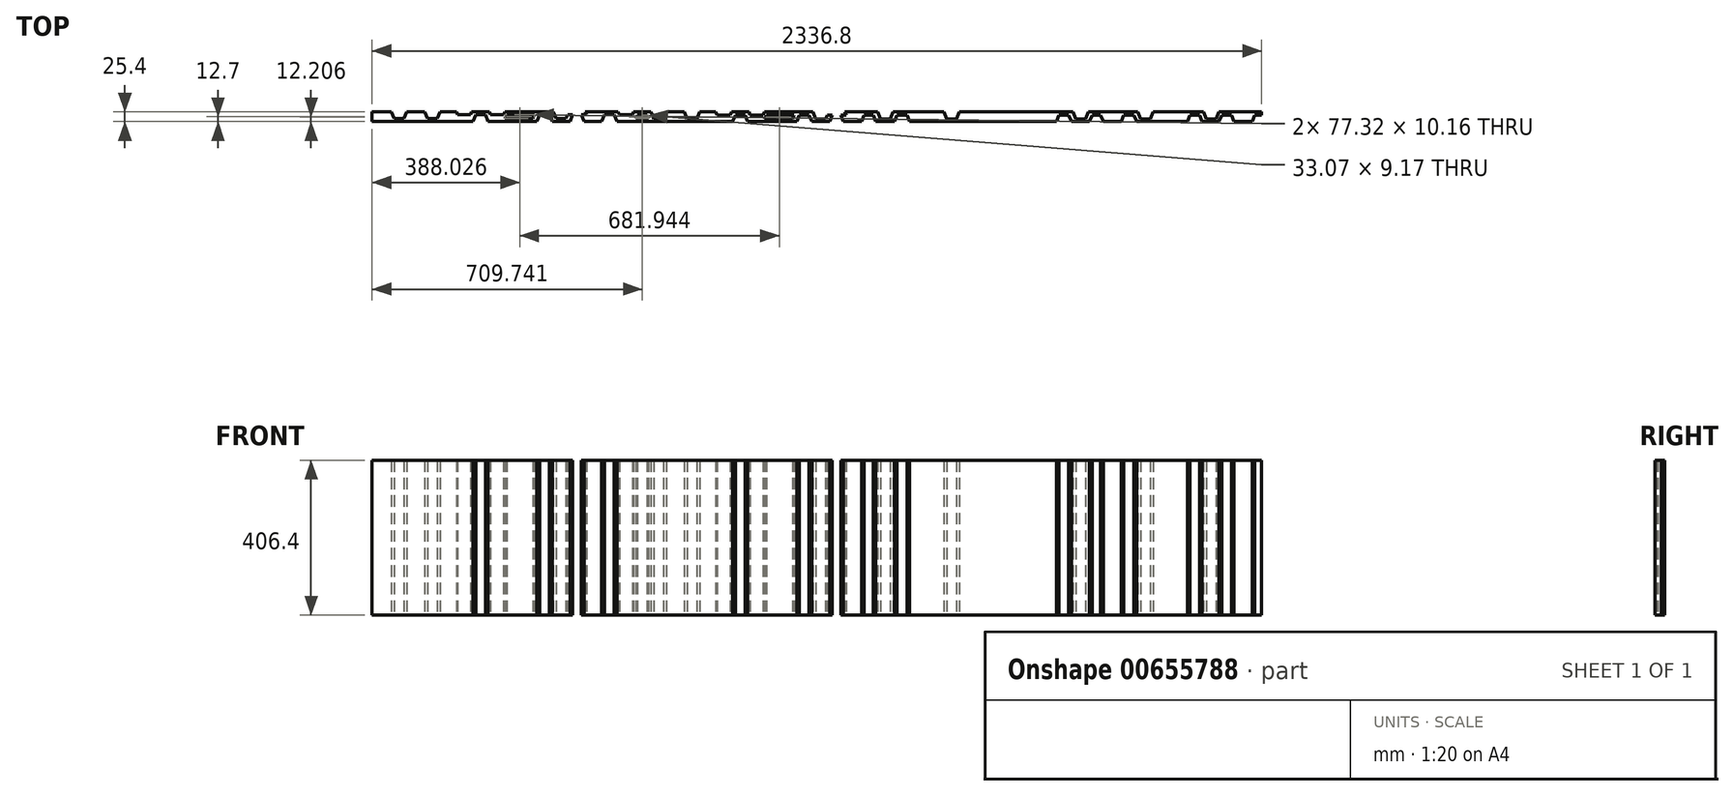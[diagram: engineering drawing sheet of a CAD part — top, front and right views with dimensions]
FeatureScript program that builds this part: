
annotation { "Feature Type Name" : "Feature", "Feature Type Description" : "" }
export const myFeature = defineFeature(function(context is Context, id is Id, definition is map)
    precondition{}
    {
        {
            var Q0;
            Q0=qCreatedBy(makeId("Front.planeOp"),FACE);
            var sketch = newSketch(context, id + "F0", { "sketchPlane" : qUnion([Q0])});
            skLineSegment(sketch, "E0.bottom", {"start": v(1168.4, 203.2) * mm, "end": v(-1168.4, 203.2) * mm});
            skLineSegment(sketch, "E0.top", {"start": v(1168.4, -203.2) * mm, "end": v(-1168.4, -203.2) * mm});
            skLineSegment(sketch, "E0.left", {"start": v(1168.4, 203.2) * mm, "end": v(1168.4, -203.2) * mm});
            skLineSegment(sketch, "E0.right", {"start": v(-1168.4, 203.2) * mm, "end": v(-1168.4, -203.2) * mm});
            skPoint(sketch, "E0.middle", {"position": v(0, 0) * mm});
            skSolve(sketch);
        }
        {
            var Q0;
            Q0=makeQuery(id+"F0.imprint","IMPRINT",FACE,{"disambiguationData":[TD([[makeQuery(id+"F0.imprint","IMPRINT",EDGE,{"derivedFrom":sQuery(id+"F0.wireOp",EDGE,"E0.bottom")}),1.0]])]});
            extrude(context, id + "F1", {"entities" : qUnion([Q0]), "depth" : 25.4 * mm, "offsetDistance" : 25.4 * mm});
        }
        {
            var Q0;
            Q0=qCreatedBy(makeId("Top.planeOp"),FACE);
            var sketch = newSketch(context, id + "F2", { "sketchPlane" : qUnion([Q0])});
            skLineSegment(sketch, "E1", {"start": v(-1153.3, -7.62) * mm, "end": v(-1114.14, -7.62) * mm});
            skLineSegment(sketch, "E2", {"start": v(-1166, -37.98) * mm, "end": v(-864.33, -37.98) * mm});
            skLineSegment(sketch, "E3", {"start": v(-1153.3, -7.62) * mm, "end": v(-1166, -37.98) * mm});
            skLineSegment(sketch, "E4", {"start": v(-1127.9, -7.62) * mm, "end": v(-1115.2, -37.98) * mm});
            skPoint(sketch, "E5.start.orphan", {"position": v(-1166, -7.62) * mm});
            skPoint(sketch, "E6.start.orphan", {"position": v(-1115.2, -7.62) * mm});
            skLineSegment(sketch, "E7", {"start": v(-1020.77, -17.78) * mm, "end": v(-1023.05, -17.78) * mm});
            skLineSegment(sketch, "E8", {"start": v(-1024.61, 10.97) * mm, "end": v(-1121.91, 10.97) * mm});
            skLineSegment(sketch, "E9", {"start": v(-1084.49, -17.78) * mm, "end": v(-1072.46, 10.97) * mm});
            skLineSegment(sketch, "E10", {"start": v(-1109.89, -17.78) * mm, "end": v(-1121.91, 10.97) * mm});
            skPoint(sketch, "E11.start.orphan", {"position": v(-1071.79, -17.78) * mm});
            skPoint(sketch, "E12.start.orphan", {"position": v(-1122.59, -17.78) * mm});
            skLineSegment(sketch, "E13", {"start": v(-1121.79, -7.62) * mm, "end": v(-1114.14, -7.62) * mm});
            skLineSegment(sketch, "E14", {"start": v(-1125.24, -37.98) * mm, "end": v(-775.72, -37.98) * mm});
            skLineSegment(sketch, "E15", {"start": v(-1066.47, -7.62) * mm, "end": v(-1079.17, -37.98) * mm});
            skLineSegment(sketch, "E16", {"start": v(-1041.07, -7.62) * mm, "end": v(-1028.37, -37.98) * mm});
            skPoint(sketch, "E17.start.orphan", {"position": v(-1077.4, -7.62) * mm});
            skPoint(sketch, "E18.start.orphan", {"position": v(-1028.37, -7.62) * mm});
            skLineSegment(sketch, "E19", {"start": v(-933.94, -17.78) * mm, "end": v(-939.72, -17.78) * mm});
            skLineSegment(sketch, "E20", {"start": v(-937.78, 10.97) * mm, "end": v(-1121.91, 10.97) * mm});
            skLineSegment(sketch, "E21", {"start": v(-997.65, -17.78) * mm, "end": v(-985.62, 10.97) * mm});
            skLineSegment(sketch, "E22", {"start": v(-1023.05, -17.78) * mm, "end": v(-1035.08, 10.97) * mm});
            skPoint(sketch, "E23.start.orphan", {"position": v(-984.95, -17.78) * mm});
            skPoint(sketch, "E24.start.orphan", {"position": v(-1035.75, -17.78) * mm});
            skLineSegment(sketch, "E25.trimOffspring", {"start": v(-1283.3, -17.78) * mm, "end": v(-1370.14, -17.78) * mm});
            skLineSegment(sketch, "E26.trimOffspring", {"start": v(-1122.59, -17.78) * mm, "end": v(-1123.65, -17.78) * mm});
            skLineSegment(sketch, "E27", {"start": v(-983.13, -7.62) * mm, "end": v(-690.86, -7.62) * mm});
            skLineSegment(sketch, "E28", {"start": v(-995.83, -37.98) * mm, "end": v(-694.16, -37.98) * mm});
            skLineSegment(sketch, "E29", {"start": v(-983.13, -7.62) * mm, "end": v(-995.83, -37.98) * mm});
            skLineSegment(sketch, "E30", {"start": v(-957.73, -7.62) * mm, "end": v(-945.03, -37.98) * mm});
            skPoint(sketch, "E31.start.orphan", {"position": v(-995.83, -7.62) * mm});
            skPoint(sketch, "E32.start.orphan", {"position": v(-945.03, -7.62) * mm});
            skLineSegment(sketch, "E33", {"start": v(-850.6, -17.78) * mm, "end": v(-939.72, -17.78) * mm});
            skLineSegment(sketch, "E34", {"start": v(-854.44, 10.97) * mm, "end": v(-951.74, 10.97) * mm});
            skLineSegment(sketch, "E35", {"start": v(-914.32, -17.78) * mm, "end": v(-902.29, 10.97) * mm});
            skLineSegment(sketch, "E36", {"start": v(-939.72, -17.78) * mm, "end": v(-951.74, 10.97) * mm});
            skPoint(sketch, "E37.start.orphan", {"position": v(-901.62, -17.78) * mm});
            skPoint(sketch, "E38.start.orphan", {"position": v(-952.42, -17.78) * mm});
            skLineSegment(sketch, "E39", {"start": v(-951.62, -7.62) * mm, "end": v(-602.26, -7.62) * mm});
            skLineSegment(sketch, "E40", {"start": v(-955.07, -37.98) * mm, "end": v(-605.55, -37.98) * mm});
            skLineSegment(sketch, "E41", {"start": v(-896.3, -7.62) * mm, "end": v(-909, -37.98) * mm});
            skLineSegment(sketch, "E42", {"start": v(-870.9, -7.62) * mm, "end": v(-858.2, -37.98) * mm});
            skPoint(sketch, "E43.start.orphan", {"position": v(-907.22, -7.62) * mm});
            skPoint(sketch, "E44.start.orphan", {"position": v(-858.2, -7.62) * mm});
            skLineSegment(sketch, "E45", {"start": v(-763.77, -17.78) * mm, "end": v(-939.72, -17.78) * mm});
            skLineSegment(sketch, "E46", {"start": v(-767.6, 10.97) * mm, "end": v(-951.74, 10.97) * mm});
            skLineSegment(sketch, "E47", {"start": v(-827.48, -17.78) * mm, "end": v(-815.45, 10.97) * mm});
            skLineSegment(sketch, "E48", {"start": v(-852.88, -17.78) * mm, "end": v(-864.91, 10.97) * mm});
            skPoint(sketch, "E49.start.orphan", {"position": v(-814.78, -17.78) * mm});
            skPoint(sketch, "E50.start.orphan", {"position": v(-865.58, -17.78) * mm});
            skLineSegment(sketch, "E51", {"start": v(-883.6, -7.62) * mm, "end": v(-883.6, -37.98) * mm});
            skLineSegment(sketch, "E52.trimOffspring", {"start": v(-952.42, -17.78) * mm, "end": v(-953.48, -17.78) * mm});
            skLineSegment(sketch, "E53.trimOffspring", {"start": v(-1080.24, -7.62) * mm, "end": v(-1077.4, -7.62) * mm});
            skLineSegment(sketch, "E54.trimOffspring", {"start": v(-1070.72, -17.78) * mm, "end": v(-1071.79, -17.78) * mm});
            skLineSegment(sketch, "E55.trimOffspring", {"start": v(-1084.49, -17.78) * mm, "end": v(-1109.89, -17.78) * mm});
            skLineSegment(sketch, "E56.trimOffspring", {"start": v(-1066.47, -7.62) * mm, "end": v(-772.43, -7.62) * mm});
            skLineSegment(sketch, "E57.trimOffspring", {"start": v(-1066.47, -7.62) * mm, "end": v(-1041.07, -7.62) * mm});
            skLineSegment(sketch, "E58.trimOffspring", {"start": v(-1035.75, -17.78) * mm, "end": v(-1036.82, -17.78) * mm});
            skLineSegment(sketch, "E59.trimOffspring", {"start": v(-1028.37, -7.62) * mm, "end": v(-861.03, -7.62) * mm});
            skLineSegment(sketch, "E60.trimOffspring", {"start": v(-997.65, -17.78) * mm, "end": v(-1023.05, -17.78) * mm});
            skLineSegment(sketch, "E61.trimOffspring", {"start": v(-984.95, -17.78) * mm, "end": v(-987.38, -17.78) * mm});
            skLineSegment(sketch, "E62", {"start": v(-814.78, -7.62) * mm, "end": v(-775.62, -7.62) * mm});
            skLineSegment(sketch, "E63", {"start": v(-827.48, -37.98) * mm, "end": v(-525.8, -37.98) * mm});
            skLineSegment(sketch, "E64", {"start": v(-814.78, -7.62) * mm, "end": v(-827.48, -37.98) * mm});
            skLineSegment(sketch, "E65", {"start": v(-789.38, -7.62) * mm, "end": v(-776.68, -37.98) * mm});
            skPoint(sketch, "E66.start.orphan", {"position": v(-827.48, -7.62) * mm});
            skPoint(sketch, "E67.start.orphan", {"position": v(-776.68, -7.62) * mm});
            skLineSegment(sketch, "E68", {"start": v(-682.25, -17.78) * mm, "end": v(-684.53, -17.78) * mm});
            skLineSegment(sketch, "E69", {"start": v(-686.1, 10.97) * mm, "end": v(-783.4, 10.97) * mm});
            skLineSegment(sketch, "E70", {"start": v(-745.97, -17.78) * mm, "end": v(-733.94, 10.97) * mm});
            skLineSegment(sketch, "E71", {"start": v(-771.37, -17.78) * mm, "end": v(-783.4, 10.97) * mm});
            skPoint(sketch, "E72.start.orphan", {"position": v(-733.27, -17.78) * mm});
            skPoint(sketch, "E73.start.orphan", {"position": v(-784.07, -17.78) * mm});
            skLineSegment(sketch, "E74", {"start": v(-783.27, -7.62) * mm, "end": v(-775.62, -7.62) * mm});
            skLineSegment(sketch, "E75", {"start": v(-786.72, -37.98) * mm, "end": v(-437.2, -37.98) * mm});
            skLineSegment(sketch, "E76", {"start": v(-727.95, -7.62) * mm, "end": v(-740.65, -37.98) * mm});
            skLineSegment(sketch, "E77", {"start": v(-702.55, -7.62) * mm, "end": v(-689.85, -37.98) * mm});
            skPoint(sketch, "E78.start.orphan", {"position": v(-738.87, -7.62) * mm});
            skPoint(sketch, "E79.start.orphan", {"position": v(-689.85, -7.62) * mm});
            skLineSegment(sketch, "E80", {"start": v(-595.42, -17.78) * mm, "end": v(-601.2, -17.78) * mm});
            skLineSegment(sketch, "E81", {"start": v(-599.26, 10.97) * mm, "end": v(-783.4, 10.97) * mm});
            skLineSegment(sketch, "E82", {"start": v(-659.13, -17.78) * mm, "end": v(-647.1, 10.97) * mm});
            skLineSegment(sketch, "E83", {"start": v(-684.53, -17.78) * mm, "end": v(-696.56, 10.97) * mm});
            skPoint(sketch, "E84.start.orphan", {"position": v(-646.43, -17.78) * mm});
            skPoint(sketch, "E85.start.orphan", {"position": v(-697.23, -17.78) * mm});
            skLineSegment(sketch, "E86.trimOffspring", {"start": v(-784.07, -17.78) * mm, "end": v(-785.13, -17.78) * mm});
            skLineSegment(sketch, "E87", {"start": v(-641.64, -8.87) * mm, "end": v(-654.34, -39.22) * mm});
            skLineSegment(sketch, "E88", {"start": v(-619.21, -7.62) * mm, "end": v(-606.51, -37.98) * mm});
            skPoint(sketch, "E89.start.orphan", {"position": v(-657.31, -7.62) * mm});
            skPoint(sketch, "E90.start.orphan", {"position": v(-606.51, -7.62) * mm});
            skLineSegment(sketch, "E91", {"start": v(-512.08, -17.78) * mm, "end": v(-601.2, -17.78) * mm});
            skLineSegment(sketch, "E92", {"start": v(-515.92, 10.97) * mm, "end": v(-613.22, 10.97) * mm});
            skLineSegment(sketch, "E93", {"start": v(-575.8, -17.78) * mm, "end": v(-563.77, 10.97) * mm});
            skLineSegment(sketch, "E94", {"start": v(-601.2, -17.78) * mm, "end": v(-613.22, 10.97) * mm});
            skPoint(sketch, "E95.start.orphan", {"position": v(-563.1, -17.78) * mm});
            skPoint(sketch, "E96.start.orphan", {"position": v(-613.9, -17.78) * mm});
            skLineSegment(sketch, "E97", {"start": v(-557.78, -7.62) * mm, "end": v(-570.48, -37.98) * mm});
            skLineSegment(sketch, "E98", {"start": v(-532.38, -7.62) * mm, "end": v(-519.68, -37.98) * mm});
            skPoint(sketch, "E99.start.orphan", {"position": v(-568.7, -7.62) * mm});
            skPoint(sketch, "E100.start.orphan", {"position": v(-519.68, -7.62) * mm});
            skLineSegment(sketch, "E101", {"start": v(-425.25, -17.78) * mm, "end": v(-601.2, -17.78) * mm});
            skLineSegment(sketch, "E102", {"start": v(-429.09, 10.97) * mm, "end": v(-613.22, 10.97) * mm});
            skLineSegment(sketch, "E103", {"start": v(-488.96, -17.78) * mm, "end": v(-476.93, 10.97) * mm});
            skLineSegment(sketch, "E104", {"start": v(-514.36, -17.78) * mm, "end": v(-526.4, 10.97) * mm});
            skPoint(sketch, "E105.start.orphan", {"position": v(-476.26, -17.78) * mm});
            skPoint(sketch, "E106.start.orphan", {"position": v(-527.06, -17.78) * mm});
            skLineSegment(sketch, "E107", {"start": v(-545.08, -7.62) * mm, "end": v(-545.08, -37.98) * mm});
            skLineSegment(sketch, "E108.trimOffspring", {"start": v(-613.9, -17.78) * mm, "end": v(-614.96, -17.78) * mm});
            skLineSegment(sketch, "E109.trimOffspring", {"start": v(-741.72, -7.62) * mm, "end": v(-738.87, -7.62) * mm});
            skLineSegment(sketch, "E110.trimOffspring", {"start": v(-732.2, -17.78) * mm, "end": v(-733.27, -17.78) * mm});
            skLineSegment(sketch, "E111.trimOffspring", {"start": v(-745.97, -17.78) * mm, "end": v(-771.37, -17.78) * mm});
            skLineSegment(sketch, "E112.trimOffspring", {"start": v(-727.95, -7.62) * mm, "end": v(-433.9, -7.62) * mm});
            skLineSegment(sketch, "E113.trimOffspring", {"start": v(-727.95, -7.62) * mm, "end": v(-702.55, -7.62) * mm});
            skLineSegment(sketch, "E114.trimOffspring", {"start": v(-697.23, -17.78) * mm, "end": v(-698.3, -17.78) * mm});
            skLineSegment(sketch, "E115.trimOffspring", {"start": v(-689.85, -7.62) * mm, "end": v(-522.51, -7.62) * mm});
            skLineSegment(sketch, "E116.trimOffspring", {"start": v(-659.13, -17.78) * mm, "end": v(-684.53, -17.78) * mm});
            skLineSegment(sketch, "E117.trimOffspring", {"start": v(-645.37, -17.78) * mm, "end": v(-646.43, -17.78) * mm});
            skLineSegment(sketch, "E118", {"start": v(-471.36, -8.6) * mm, "end": v(-432.2, -8.6) * mm});
            skLineSegment(sketch, "E119", {"start": v(-484.06, -38.97) * mm, "end": v(-182.39, -38.97) * mm});
            skLineSegment(sketch, "E120", {"start": v(-471.36, -8.6) * mm, "end": v(-484.06, -38.97) * mm});
            skLineSegment(sketch, "E121", {"start": v(-445.96, -8.6) * mm, "end": v(-433.26, -38.97) * mm});
            skPoint(sketch, "E122.start.orphan", {"position": v(-484.06, -8.6) * mm});
            skPoint(sketch, "E123.start.orphan", {"position": v(-433.26, -8.6) * mm});
            skLineSegment(sketch, "E124", {"start": v(-338.83, -18.77) * mm, "end": v(-341.1, -18.77) * mm});
            skLineSegment(sketch, "E125", {"start": v(-342.67, 9.98) * mm, "end": v(-439.97, 9.98) * mm});
            skLineSegment(sketch, "E126", {"start": v(-402.54, -18.77) * mm, "end": v(-390.51, 9.98) * mm});
            skLineSegment(sketch, "E127", {"start": v(-427.94, -18.77) * mm, "end": v(-439.97, 9.98) * mm});
            skPoint(sketch, "E128.start.orphan", {"position": v(-389.84, -18.77) * mm});
            skPoint(sketch, "E129.start.orphan", {"position": v(-440.64, -18.77) * mm});
            skLineSegment(sketch, "E130", {"start": v(-439.84, -8.6) * mm, "end": v(-432.2, -8.6) * mm});
            skLineSegment(sketch, "E131", {"start": v(-443.3, -38.97) * mm, "end": v(-93.78, -38.97) * mm});
            skLineSegment(sketch, "E132", {"start": v(-384.52, -8.6) * mm, "end": v(-397.22, -38.97) * mm});
            skLineSegment(sketch, "E133", {"start": v(-359.12, -8.6) * mm, "end": v(-346.42, -38.97) * mm});
            skPoint(sketch, "E134.start.orphan", {"position": v(-395.45, -8.6) * mm});
            skPoint(sketch, "E135.start.orphan", {"position": v(-346.42, -8.6) * mm});
            skLineSegment(sketch, "E136", {"start": v(-252, -18.77) * mm, "end": v(-257.77, -18.77) * mm});
            skLineSegment(sketch, "E137", {"start": v(-255.83, 9.98) * mm, "end": v(-439.97, 9.98) * mm});
            skLineSegment(sketch, "E138", {"start": v(-315.7, -18.77) * mm, "end": v(-303.68, 9.98) * mm});
            skLineSegment(sketch, "E139", {"start": v(-341.1, -18.77) * mm, "end": v(-353.14, 9.98) * mm});
            skPoint(sketch, "E140.start.orphan", {"position": v(-303, -18.77) * mm});
            skPoint(sketch, "E141.start.orphan", {"position": v(-353.8, -18.77) * mm});
            skLineSegment(sketch, "E142.trimOffspring", {"start": v(-440.64, -18.77) * mm, "end": v(-441.7, -18.77) * mm});
            skLineSegment(sketch, "E143", {"start": v(-301.19, -8.6) * mm, "end": v(-8.92, -8.6) * mm});
            skLineSegment(sketch, "E144", {"start": v(-313.89, -38.97) * mm, "end": v(-12.22, -38.97) * mm});
            skLineSegment(sketch, "E145", {"start": v(-301.19, -8.6) * mm, "end": v(-313.89, -38.97) * mm});
            skLineSegment(sketch, "E146", {"start": v(-275.79, -8.6) * mm, "end": v(-263.09, -38.97) * mm});
            skPoint(sketch, "E147.start.orphan", {"position": v(-313.89, -8.6) * mm});
            skPoint(sketch, "E148.start.orphan", {"position": v(-263.09, -8.6) * mm});
            skLineSegment(sketch, "E149", {"start": v(-168.66, -18.77) * mm, "end": v(-257.77, -18.77) * mm});
            skLineSegment(sketch, "E150", {"start": v(-172.5, 9.98) * mm, "end": v(-269.8, 9.98) * mm});
            skLineSegment(sketch, "E151", {"start": v(-232.37, -18.77) * mm, "end": v(-220.34, 9.98) * mm});
            skLineSegment(sketch, "E152", {"start": v(-257.77, -18.77) * mm, "end": v(-269.8, 9.98) * mm});
            skPoint(sketch, "E153.start.orphan", {"position": v(-219.67, -18.77) * mm});
            skPoint(sketch, "E154.start.orphan", {"position": v(-270.47, -18.77) * mm});
            skLineSegment(sketch, "E155", {"start": v(-269.68, -8.6) * mm, "end": v(79.69, -8.6) * mm});
            skLineSegment(sketch, "E156", {"start": v(-273.13, -38.97) * mm, "end": v(76.4, -38.97) * mm});
            skLineSegment(sketch, "E157", {"start": v(-214.36, -8.6) * mm, "end": v(-227.06, -38.97) * mm});
            skLineSegment(sketch, "E158", {"start": v(-188.96, -8.6) * mm, "end": v(-176.26, -38.97) * mm});
            skPoint(sketch, "E159.start.orphan", {"position": v(-225.28, -8.6) * mm});
            skPoint(sketch, "E160.start.orphan", {"position": v(-176.26, -8.6) * mm});
            skLineSegment(sketch, "E161", {"start": v(-81.83, -18.77) * mm, "end": v(-257.77, -18.77) * mm});
            skLineSegment(sketch, "E162", {"start": v(-85.66, 9.98) * mm, "end": v(-269.8, 9.98) * mm});
            skLineSegment(sketch, "E163", {"start": v(-145.54, -18.77) * mm, "end": v(-133.5, 9.98) * mm});
            skLineSegment(sketch, "E164", {"start": v(-170.94, -18.77) * mm, "end": v(-182.97, 9.98) * mm});
            skPoint(sketch, "E165.start.orphan", {"position": v(-132.84, -18.77) * mm});
            skPoint(sketch, "E166.start.orphan", {"position": v(-183.64, -18.77) * mm});
            skLineSegment(sketch, "E167", {"start": v(-201.66, -8.6) * mm, "end": v(-201.66, -38.97) * mm});
            skLineSegment(sketch, "E168.trimOffspring", {"start": v(-270.47, -18.77) * mm, "end": v(-271.54, -18.77) * mm});
            skLineSegment(sketch, "E169.trimOffspring", {"start": v(-398.3, -8.6) * mm, "end": v(-395.45, -8.6) * mm});
            skLineSegment(sketch, "E170.trimOffspring", {"start": v(-388.78, -18.77) * mm, "end": v(-389.84, -18.77) * mm});
            skLineSegment(sketch, "E171.trimOffspring", {"start": v(-402.54, -18.77) * mm, "end": v(-427.94, -18.77) * mm});
            skLineSegment(sketch, "E172.trimOffspring", {"start": v(-384.52, -8.6) * mm, "end": v(-90.48, -8.6) * mm});
            skLineSegment(sketch, "E173.trimOffspring", {"start": v(-384.52, -8.6) * mm, "end": v(-359.12, -8.6) * mm});
            skLineSegment(sketch, "E174.trimOffspring", {"start": v(-353.8, -18.77) * mm, "end": v(-354.87, -18.77) * mm});
            skLineSegment(sketch, "E175.trimOffspring", {"start": v(-346.42, -8.6) * mm, "end": v(-179.1, -8.6) * mm});
            skLineSegment(sketch, "E176.trimOffspring", {"start": v(-315.7, -18.77) * mm, "end": v(-341.1, -18.77) * mm});
            skLineSegment(sketch, "E177.trimOffspring", {"start": v(-303, -18.77) * mm, "end": v(-305.44, -18.77) * mm});
            skLineSegment(sketch, "E178", {"start": v(-132.84, -8.6) * mm, "end": v(-93.67, -8.6) * mm});
            skLineSegment(sketch, "E179", {"start": v(-145.54, -38.97) * mm, "end": v(156.14, -38.97) * mm});
            skLineSegment(sketch, "E180", {"start": v(-132.84, -8.6) * mm, "end": v(-145.54, -38.97) * mm});
            skLineSegment(sketch, "E181", {"start": v(-107.44, -8.6) * mm, "end": v(-94.74, -38.97) * mm});
            skPoint(sketch, "E182.start.orphan", {"position": v(-145.54, -8.6) * mm});
            skPoint(sketch, "E183.start.orphan", {"position": v(-94.74, -8.6) * mm});
            skLineSegment(sketch, "E184", {"start": v(-0.3, -18.77) * mm, "end": v(-2.59, -18.77) * mm});
            skLineSegment(sketch, "E185", {"start": v(-4.15, 9.98) * mm, "end": v(-101.45, 9.98) * mm});
            skLineSegment(sketch, "E186", {"start": v(-64.02, -18.77) * mm, "end": v(-52, 9.98) * mm});
            skLineSegment(sketch, "E187", {"start": v(-89.42, -18.77) * mm, "end": v(-101.45, 9.98) * mm});
            skPoint(sketch, "E188.start.orphan", {"position": v(-51.32, -18.77) * mm});
            skPoint(sketch, "E189.start.orphan", {"position": v(-102.12, -18.77) * mm});
            skLineSegment(sketch, "E190", {"start": v(-101.32, -8.6) * mm, "end": v(-93.67, -8.6) * mm});
            skLineSegment(sketch, "E191", {"start": v(-104.78, -38.97) * mm, "end": v(244.74, -38.97) * mm});
            skLineSegment(sketch, "E192", {"start": v(-46, -8.6) * mm, "end": v(-58.7, -38.97) * mm});
            skLineSegment(sketch, "E193", {"start": v(-20.6, -8.6) * mm, "end": v(-7.9, -38.97) * mm});
            skPoint(sketch, "E194.start.orphan", {"position": v(-56.93, -8.6) * mm});
            skPoint(sketch, "E195.start.orphan", {"position": v(-7.9, -8.6) * mm});
            skLineSegment(sketch, "E196", {"start": v(86.52, -18.77) * mm, "end": v(80.75, -18.77) * mm});
            skLineSegment(sketch, "E197", {"start": v(82.69, 9.98) * mm, "end": v(-101.45, 9.98) * mm});
            skLineSegment(sketch, "E198", {"start": v(22.81, -18.77) * mm, "end": v(34.84, 9.98) * mm});
            skLineSegment(sketch, "E199", {"start": v(-2.59, -18.77) * mm, "end": v(-14.62, 9.98) * mm});
            skPoint(sketch, "E200.start.orphan", {"position": v(35.51, -18.77) * mm});
            skPoint(sketch, "E201.start.orphan", {"position": v(-15.29, -18.77) * mm});
            skLineSegment(sketch, "E202.trimOffspring", {"start": v(-102.12, -18.77) * mm, "end": v(-103.19, -18.77) * mm});
            skLineSegment(sketch, "E203", {"start": v(40.3, -9.85) * mm, "end": v(27.6, -40.21) * mm});
            skLineSegment(sketch, "E204", {"start": v(62.73, -8.6) * mm, "end": v(75.43, -38.97) * mm});
            skPoint(sketch, "E205.start.orphan", {"position": v(22.27, -7.62) * mm});
            skPoint(sketch, "E206.start.orphan", {"position": v(73.07, -7.62) * mm});
            skLineSegment(sketch, "E207", {"start": v(169.86, -18.77) * mm, "end": v(80.75, -18.77) * mm});
            skLineSegment(sketch, "E208", {"start": v(166.02, 9.98) * mm, "end": v(68.72, 9.98) * mm});
            skLineSegment(sketch, "E209", {"start": v(106.15, -18.77) * mm, "end": v(118.18, 9.98) * mm});
            skLineSegment(sketch, "E210", {"start": v(80.75, -18.77) * mm, "end": v(68.72, 9.98) * mm});
            skPoint(sketch, "E211.start.orphan", {"position": v(118.85, -18.77) * mm});
            skPoint(sketch, "E212.start.orphan", {"position": v(68.05, -18.77) * mm});
            skLineSegment(sketch, "E213", {"start": v(124.17, -8.6) * mm, "end": v(111.47, -38.97) * mm});
            skLineSegment(sketch, "E214", {"start": v(147.2, -7.62) * mm, "end": v(159.9, -37.98) * mm});
            skPoint(sketch, "E215.start.orphan", {"position": v(110.88, -7.62) * mm});
            skPoint(sketch, "E216.start.orphan", {"position": v(159.9, -7.62) * mm});
            skLineSegment(sketch, "E217", {"start": v(256.7, -18.77) * mm, "end": v(80.75, -18.77) * mm});
            skLineSegment(sketch, "E218", {"start": v(252.86, 9.98) * mm, "end": v(68.72, 9.98) * mm});
            skLineSegment(sketch, "E219", {"start": v(192.98, -18.77) * mm, "end": v(205.01, 9.98) * mm});
            skLineSegment(sketch, "E220", {"start": v(167.58, -18.77) * mm, "end": v(155.55, 9.98) * mm});
            skPoint(sketch, "E221.start.orphan", {"position": v(205.68, -18.77) * mm});
            skPoint(sketch, "E222.start.orphan", {"position": v(154.88, -18.77) * mm});
            skLineSegment(sketch, "E223", {"start": v(134.5, -7.62) * mm, "end": v(134.5, -37.98) * mm});
            skLineSegment(sketch, "E224.trimOffspring", {"start": v(68.05, -18.77) * mm, "end": v(66.98, -18.77) * mm});
            skLineSegment(sketch, "E225.trimOffspring", {"start": v(-59.77, -8.6) * mm, "end": v(-56.93, -8.6) * mm});
            skLineSegment(sketch, "E226.trimOffspring", {"start": v(-50.26, -18.77) * mm, "end": v(-51.32, -18.77) * mm});
            skLineSegment(sketch, "E227.trimOffspring", {"start": v(-64.02, -18.77) * mm, "end": v(-89.42, -18.77) * mm});
            skLineSegment(sketch, "E228.trimOffspring", {"start": v(-46, -8.6) * mm, "end": v(248.04, -8.6) * mm});
            skLineSegment(sketch, "E229.trimOffspring", {"start": v(-46, -8.6) * mm, "end": v(-20.6, -8.6) * mm});
            skLineSegment(sketch, "E230.trimOffspring", {"start": v(-15.29, -18.77) * mm, "end": v(-16.35, -18.77) * mm});
            skLineSegment(sketch, "E231.trimOffspring", {"start": v(-7.9, -8.6) * mm, "end": v(159.43, -8.6) * mm});
            skLineSegment(sketch, "E232.trimOffspring", {"start": v(22.81, -18.77) * mm, "end": v(-2.59, -18.77) * mm});
            skLineSegment(sketch, "E233.trimOffspring", {"start": v(36.58, -18.77) * mm, "end": v(35.51, -18.77) * mm});
            skLineSegment(sketch, "E234", {"start": v(211.15, -8.24) * mm, "end": v(250.32, -8.24) * mm});
            skLineSegment(sketch, "E235", {"start": v(198.45, -38.6) * mm, "end": v(500.13, -38.6) * mm});
            skLineSegment(sketch, "E236", {"start": v(211.15, -8.24) * mm, "end": v(198.45, -38.6) * mm});
            skLineSegment(sketch, "E237", {"start": v(236.55, -8.24) * mm, "end": v(249.25, -38.6) * mm});
            skPoint(sketch, "E238.start.orphan", {"position": v(198.45, -8.24) * mm});
            skPoint(sketch, "E239.start.orphan", {"position": v(249.25, -8.24) * mm});
            skLineSegment(sketch, "E240", {"start": v(343.68, -18.4) * mm, "end": v(341.4, -18.4) * mm});
            skLineSegment(sketch, "E241", {"start": v(339.84, 10.35) * mm, "end": v(242.54, 10.35) * mm});
            skLineSegment(sketch, "E242", {"start": v(279.97, -18.4) * mm, "end": v(292, 10.35) * mm});
            skLineSegment(sketch, "E243", {"start": v(254.57, -18.4) * mm, "end": v(242.54, 10.35) * mm});
            skPoint(sketch, "E244.start.orphan", {"position": v(292.67, -18.4) * mm});
            skPoint(sketch, "E245.start.orphan", {"position": v(241.87, -18.4) * mm});
            skLineSegment(sketch, "E246", {"start": v(242.67, -8.24) * mm, "end": v(250.32, -8.24) * mm});
            skLineSegment(sketch, "E247", {"start": v(239.22, -38.6) * mm, "end": v(588.74, -38.6) * mm});
            skLineSegment(sketch, "E248", {"start": v(297.99, -8.24) * mm, "end": v(285.29, -38.6) * mm});
            skLineSegment(sketch, "E249", {"start": v(323.39, -8.24) * mm, "end": v(336.09, -38.6) * mm});
            skPoint(sketch, "E250.start.orphan", {"position": v(287.06, -8.24) * mm});
            skPoint(sketch, "E251.start.orphan", {"position": v(336.09, -8.24) * mm});
            skLineSegment(sketch, "E252", {"start": v(430.52, -18.4) * mm, "end": v(424.74, -18.4) * mm});
            skLineSegment(sketch, "E253", {"start": v(426.68, 10.35) * mm, "end": v(242.54, 10.35) * mm});
            skLineSegment(sketch, "E254", {"start": v(366.8, -18.4) * mm, "end": v(378.83, 10.35) * mm});
            skLineSegment(sketch, "E255", {"start": v(341.4, -18.4) * mm, "end": v(329.37, 10.35) * mm});
            skPoint(sketch, "E256.start.orphan", {"position": v(379.5, -18.4) * mm});
            skPoint(sketch, "E257.start.orphan", {"position": v(328.7, -18.4) * mm});
            skLineSegment(sketch, "E258.trimOffspring", {"start": v(241.87, -18.4) * mm, "end": v(240.8, -18.4) * mm});
            skLineSegment(sketch, "E259", {"start": v(381.32, -8.24) * mm, "end": v(420.49, -8.24) * mm});
            skLineSegment(sketch, "E260", {"start": v(368.62, -38.6) * mm, "end": v(670.3, -38.6) * mm});
            skLineSegment(sketch, "E261", {"start": v(381.32, -8.24) * mm, "end": v(368.62, -38.6) * mm});
            skLineSegment(sketch, "E262", {"start": v(406.72, -8.24) * mm, "end": v(419.42, -38.6) * mm});
            skPoint(sketch, "E263.start.orphan", {"position": v(368.62, -8.24) * mm});
            skPoint(sketch, "E264.start.orphan", {"position": v(419.42, -8.24) * mm});
            skLineSegment(sketch, "E265", {"start": v(513.85, -18.4) * mm, "end": v(497.8, -18.4) * mm});
            skLineSegment(sketch, "E266", {"start": v(510.01, 10.35) * mm, "end": v(412.71, 10.35) * mm});
            skLineSegment(sketch, "E267", {"start": v(450.14, -18.4) * mm, "end": v(462.17, 10.35) * mm});
            skLineSegment(sketch, "E268", {"start": v(424.74, -18.4) * mm, "end": v(412.71, 10.35) * mm});
            skPoint(sketch, "E269.start.orphan", {"position": v(462.84, -18.4) * mm});
            skPoint(sketch, "E270.start.orphan", {"position": v(412.04, -18.4) * mm});
            skLineSegment(sketch, "E271", {"start": v(412.84, -8.24) * mm, "end": v(420.49, -8.24) * mm});
            skLineSegment(sketch, "E272", {"start": v(409.39, -38.6) * mm, "end": v(758.9, -38.6) * mm});
            skLineSegment(sketch, "E273", {"start": v(468.16, -8.24) * mm, "end": v(455.46, -38.6) * mm});
            skLineSegment(sketch, "E274", {"start": v(493.56, -8.24) * mm, "end": v(506.26, -38.6) * mm});
            skPoint(sketch, "E275.start.orphan", {"position": v(457.23, -8.24) * mm});
            skPoint(sketch, "E276.start.orphan", {"position": v(506.26, -8.24) * mm});
            skLineSegment(sketch, "E277", {"start": v(600.68, -18.4) * mm, "end": v(579.32, -18.4) * mm});
            skLineSegment(sketch, "E278", {"start": v(596.85, 10.35) * mm, "end": v(412.71, 10.35) * mm});
            skLineSegment(sketch, "E279", {"start": v(536.97, -18.4) * mm, "end": v(549, 10.35) * mm});
            skLineSegment(sketch, "E280", {"start": v(511.57, -18.4) * mm, "end": v(499.54, 10.35) * mm});
            skPoint(sketch, "E281.start.orphan", {"position": v(549.67, -18.4) * mm});
            skPoint(sketch, "E282.start.orphan", {"position": v(498.87, -18.4) * mm});
            skLineSegment(sketch, "E283.trimOffspring", {"start": v(412.04, -18.4) * mm, "end": v(410.97, -18.4) * mm});
            skLineSegment(sketch, "E284.trimOffspring", {"start": v(284.22, -8.24) * mm, "end": v(287.06, -8.24) * mm});
            skLineSegment(sketch, "E285.trimOffspring", {"start": v(293.74, -18.4) * mm, "end": v(292.67, -18.4) * mm});
            skLineSegment(sketch, "E286.trimOffspring", {"start": v(279.97, -18.4) * mm, "end": v(254.57, -18.4) * mm});
            skLineSegment(sketch, "E287.trimOffspring", {"start": v(297.99, -8.24) * mm, "end": v(420.49, -8.24) * mm});
            skLineSegment(sketch, "E288.trimOffspring", {"start": v(297.99, -8.24) * mm, "end": v(323.39, -8.24) * mm});
            skLineSegment(sketch, "E289.trimOffspring", {"start": v(328.7, -18.4) * mm, "end": v(327.64, -18.4) * mm});
            skLineSegment(sketch, "E290.trimOffspring", {"start": v(336.09, -8.24) * mm, "end": v(337.15, -8.24) * mm});
            skLineSegment(sketch, "E291.trimOffspring", {"start": v(366.8, -18.4) * mm, "end": v(341.4, -18.4) * mm});
            skLineSegment(sketch, "E292.trimOffspring", {"start": v(379.5, -18.4) * mm, "end": v(377.07, -18.4) * mm});
            skLineSegment(sketch, "E293", {"start": v(549.67, -8.24) * mm, "end": v(588.84, -8.24) * mm});
            skLineSegment(sketch, "E294", {"start": v(536.97, -38.6) * mm, "end": v(838.65, -38.6) * mm});
            skLineSegment(sketch, "E295", {"start": v(549.67, -8.24) * mm, "end": v(536.97, -38.6) * mm});
            skLineSegment(sketch, "E296", {"start": v(575.07, -8.24) * mm, "end": v(587.77, -38.6) * mm});
            skPoint(sketch, "E297.start.orphan", {"position": v(536.97, -8.24) * mm});
            skPoint(sketch, "E298.start.orphan", {"position": v(587.77, -8.24) * mm});
            skLineSegment(sketch, "E299", {"start": v(682.2, -18.4) * mm, "end": v(679.92, -18.4) * mm});
            skLineSegment(sketch, "E300", {"start": v(678.36, 10.35) * mm, "end": v(581.06, 10.35) * mm});
            skLineSegment(sketch, "E301", {"start": v(618.49, -18.4) * mm, "end": v(630.52, 10.35) * mm});
            skLineSegment(sketch, "E302", {"start": v(593.09, -18.4) * mm, "end": v(581.06, 10.35) * mm});
            skPoint(sketch, "E303.start.orphan", {"position": v(631.19, -18.4) * mm});
            skPoint(sketch, "E304.start.orphan", {"position": v(580.39, -18.4) * mm});
            skLineSegment(sketch, "E305", {"start": v(581.19, -8.24) * mm, "end": v(588.84, -8.24) * mm});
            skLineSegment(sketch, "E306", {"start": v(577.74, -38.6) * mm, "end": v(927.26, -38.6) * mm});
            skLineSegment(sketch, "E307", {"start": v(636.5, -8.24) * mm, "end": v(623.8, -38.6) * mm});
            skLineSegment(sketch, "E308", {"start": v(661.9, -8.24) * mm, "end": v(674.6, -38.6) * mm});
            skPoint(sketch, "E309.start.orphan", {"position": v(625.58, -8.24) * mm});
            skPoint(sketch, "E310.start.orphan", {"position": v(674.6, -8.24) * mm});
            skLineSegment(sketch, "E311", {"start": v(769.04, -18.4) * mm, "end": v(763.26, -18.4) * mm});
            skLineSegment(sketch, "E312", {"start": v(765.2, 10.35) * mm, "end": v(581.06, 10.35) * mm});
            skLineSegment(sketch, "E313", {"start": v(705.32, -18.4) * mm, "end": v(717.35, 10.35) * mm});
            skLineSegment(sketch, "E314", {"start": v(679.92, -18.4) * mm, "end": v(667.9, 10.35) * mm});
            skPoint(sketch, "E315.start.orphan", {"position": v(718.02, -18.4) * mm});
            skPoint(sketch, "E316.start.orphan", {"position": v(667.22, -18.4) * mm});
            skLineSegment(sketch, "E317.trimOffspring", {"start": v(580.39, -18.4) * mm, "end": v(579.32, -18.4) * mm});
            skLineSegment(sketch, "E318", {"start": v(722.82, -9.49) * mm, "end": v(710.12, -39.84) * mm});
            skLineSegment(sketch, "E319", {"start": v(745.24, -8.24) * mm, "end": v(757.94, -38.6) * mm});
            skPoint(sketch, "E320.start.orphan", {"position": v(708.02, -8.6) * mm});
            skPoint(sketch, "E321.start.orphan", {"position": v(758.82, -8.6) * mm});
            skLineSegment(sketch, "E322", {"start": v(852.37, -18.4) * mm, "end": v(837.05, -18.4) * mm});
            skLineSegment(sketch, "E323", {"start": v(848.53, 10.35) * mm, "end": v(751.23, 10.35) * mm});
            skLineSegment(sketch, "E324", {"start": v(788.66, -18.4) * mm, "end": v(800.69, 10.35) * mm});
            skLineSegment(sketch, "E325", {"start": v(763.26, -18.4) * mm, "end": v(751.23, 10.35) * mm});
            skPoint(sketch, "E326.start.orphan", {"position": v(801.36, -18.4) * mm});
            skPoint(sketch, "E327.start.orphan", {"position": v(750.56, -18.4) * mm});
            skLineSegment(sketch, "E328", {"start": v(806.68, -8.24) * mm, "end": v(793.98, -38.6) * mm});
            skLineSegment(sketch, "E329", {"start": v(832.96, -8.6) * mm, "end": v(845.66, -38.97) * mm});
            skPoint(sketch, "E330.start.orphan", {"position": v(796.63, -8.6) * mm});
            skPoint(sketch, "E331.start.orphan", {"position": v(845.66, -8.6) * mm});
            skLineSegment(sketch, "E332", {"start": v(939.2, -18.4) * mm, "end": v(922.33, -18.4) * mm});
            skLineSegment(sketch, "E333", {"start": v(935.37, 10.35) * mm, "end": v(751.23, 10.35) * mm});
            skLineSegment(sketch, "E334", {"start": v(875.5, -18.4) * mm, "end": v(887.52, 10.35) * mm});
            skLineSegment(sketch, "E335", {"start": v(850.1, -18.4) * mm, "end": v(838.06, 10.35) * mm});
            skPoint(sketch, "E336.start.orphan", {"position": v(888.2, -18.4) * mm});
            skPoint(sketch, "E337.start.orphan", {"position": v(837.4, -18.4) * mm});
            skLineSegment(sketch, "E338.trimOffspring", {"start": v(750.56, -18.4) * mm, "end": v(749.5, -18.4) * mm});
            skLineSegment(sketch, "E339.trimOffspring", {"start": v(622.74, -8.24) * mm, "end": v(625.58, -8.24) * mm});
            skLineSegment(sketch, "E340.trimOffspring", {"start": v(632.26, -18.4) * mm, "end": v(631.19, -18.4) * mm});
            skLineSegment(sketch, "E341.trimOffspring", {"start": v(618.49, -18.4) * mm, "end": v(593.09, -18.4) * mm});
            skLineSegment(sketch, "E342.trimOffspring", {"start": v(636.5, -8.24) * mm, "end": v(675.67, -8.24) * mm});
            skLineSegment(sketch, "E343.trimOffspring", {"start": v(636.5, -8.24) * mm, "end": v(661.9, -8.24) * mm});
            skLineSegment(sketch, "E344.trimOffspring", {"start": v(667.22, -18.4) * mm, "end": v(666.16, -18.4) * mm});
            skLineSegment(sketch, "E345.trimOffspring", {"start": v(674.6, -8.24) * mm, "end": v(675.67, -8.24) * mm});
            skLineSegment(sketch, "E346.trimOffspring", {"start": v(705.32, -18.4) * mm, "end": v(679.92, -18.4) * mm});
            skLineSegment(sketch, "E347.trimOffspring", {"start": v(719.1, -18.4) * mm, "end": v(718.02, -18.4) * mm});
            skLineSegment(sketch, "E348", {"start": v(893.1, -9.23) * mm, "end": v(932.26, -9.23) * mm});
            skLineSegment(sketch, "E349", {"start": v(880.4, -39.59) * mm, "end": v(1182.07, -39.59) * mm});
            skLineSegment(sketch, "E350", {"start": v(893.1, -9.23) * mm, "end": v(880.4, -39.59) * mm});
            skLineSegment(sketch, "E351", {"start": v(918.5, -9.23) * mm, "end": v(931.2, -39.59) * mm});
            skPoint(sketch, "E352.start.orphan", {"position": v(880.4, -9.23) * mm});
            skPoint(sketch, "E353.start.orphan", {"position": v(931.2, -9.23) * mm});
            skLineSegment(sketch, "E354", {"start": v(1025.63, -19.39) * mm, "end": v(1023.35, -19.39) * mm});
            skLineSegment(sketch, "E355", {"start": v(1021.79, 9.36) * mm, "end": v(924.48, 9.36) * mm});
            skLineSegment(sketch, "E356", {"start": v(961.91, -19.39) * mm, "end": v(973.94, 9.36) * mm});
            skLineSegment(sketch, "E357", {"start": v(936.51, -19.39) * mm, "end": v(924.48, 9.36) * mm});
            skPoint(sketch, "E358.start.orphan", {"position": v(974.61, -19.39) * mm});
            skPoint(sketch, "E359.start.orphan", {"position": v(923.81, -19.39) * mm});
            skLineSegment(sketch, "E360", {"start": v(924.61, -9.23) * mm, "end": v(932.26, -9.23) * mm});
            skLineSegment(sketch, "E361", {"start": v(921.16, -39.59) * mm, "end": v(1270.68, -39.59) * mm});
            skLineSegment(sketch, "E362", {"start": v(979.93, -9.23) * mm, "end": v(967.23, -39.59) * mm});
            skLineSegment(sketch, "E363", {"start": v(1005.33, -9.23) * mm, "end": v(1018.03, -39.59) * mm});
            skPoint(sketch, "E364.start.orphan", {"position": v(969, -9.23) * mm});
            skPoint(sketch, "E365.start.orphan", {"position": v(1018.03, -9.23) * mm});
            skLineSegment(sketch, "E366", {"start": v(1112.46, -19.39) * mm, "end": v(1106.68, -19.39) * mm});
            skLineSegment(sketch, "E367", {"start": v(1108.62, 9.36) * mm, "end": v(924.48, 9.36) * mm});
            skLineSegment(sketch, "E368", {"start": v(1048.75, -19.39) * mm, "end": v(1060.78, 9.36) * mm});
            skLineSegment(sketch, "E369", {"start": v(1023.35, -19.39) * mm, "end": v(1011.32, 9.36) * mm});
            skPoint(sketch, "E370.start.orphan", {"position": v(1061.45, -19.39) * mm});
            skPoint(sketch, "E371.start.orphan", {"position": v(1010.65, -19.39) * mm});
            skLineSegment(sketch, "E372.trimOffspring", {"start": v(923.81, -19.39) * mm, "end": v(922.75, -19.39) * mm});
            skLineSegment(sketch, "E373", {"start": v(1063.27, -9.23) * mm, "end": v(1102.43, -9.23) * mm});
            skLineSegment(sketch, "E374", {"start": v(1050.57, -39.59) * mm, "end": v(1352.24, -39.59) * mm});
            skLineSegment(sketch, "E375", {"start": v(1063.27, -9.23) * mm, "end": v(1050.57, -39.59) * mm});
            skLineSegment(sketch, "E376", {"start": v(1088.67, -9.23) * mm, "end": v(1101.37, -39.59) * mm});
            skPoint(sketch, "E377.start.orphan", {"position": v(1050.57, -9.23) * mm});
            skPoint(sketch, "E378.start.orphan", {"position": v(1101.37, -9.23) * mm});
            skLineSegment(sketch, "E379", {"start": v(1195.8, -19.39) * mm, "end": v(1179.75, -19.39) * mm});
            skLineSegment(sketch, "E380", {"start": v(1191.96, 9.36) * mm, "end": v(1094.65, 9.36) * mm});
            skLineSegment(sketch, "E381", {"start": v(1132.08, -19.39) * mm, "end": v(1144.11, 9.36) * mm});
            skLineSegment(sketch, "E382", {"start": v(1106.68, -19.39) * mm, "end": v(1094.65, 9.36) * mm});
            skPoint(sketch, "E383.start.orphan", {"position": v(1144.78, -19.39) * mm});
            skPoint(sketch, "E384.start.orphan", {"position": v(1093.98, -19.39) * mm});
            skLineSegment(sketch, "E385", {"start": v(1094.78, -9.23) * mm, "end": v(1102.43, -9.23) * mm});
            skLineSegment(sketch, "E386", {"start": v(1091.33, -39.59) * mm, "end": v(1440.85, -39.59) * mm});
            skLineSegment(sketch, "E387", {"start": v(1150.1, -9.23) * mm, "end": v(1137.4, -39.59) * mm});
            skLineSegment(sketch, "E388", {"start": v(1175.5, -9.23) * mm, "end": v(1188.2, -39.59) * mm});
            skPoint(sketch, "E389.start.orphan", {"position": v(1139.18, -9.23) * mm});
            skPoint(sketch, "E390.start.orphan", {"position": v(1188.2, -9.23) * mm});
            skLineSegment(sketch, "E391", {"start": v(1282.63, -19.39) * mm, "end": v(1179.75, -19.39) * mm});
            skLineSegment(sketch, "E392", {"start": v(1278.8, 9.36) * mm, "end": v(1094.65, 9.36) * mm});
            skLineSegment(sketch, "E393", {"start": v(1193.52, -19.39) * mm, "end": v(1181.49, 9.36) * mm});
            skPoint(sketch, "E394.start.orphan", {"position": v(1180.82, -19.39) * mm});
            skLineSegment(sketch, "E395.trimOffspring", {"start": v(1093.98, -19.39) * mm, "end": v(1092.92, -19.39) * mm});
            skLineSegment(sketch, "E396.trimOffspring", {"start": v(966.16, -9.23) * mm, "end": v(969, -9.23) * mm});
            skLineSegment(sketch, "E397.trimOffspring", {"start": v(975.68, -19.39) * mm, "end": v(974.61, -19.39) * mm});
            skLineSegment(sketch, "E398.trimOffspring", {"start": v(961.91, -19.39) * mm, "end": v(936.51, -19.39) * mm});
            skLineSegment(sketch, "E399.trimOffspring", {"start": v(979.93, -9.23) * mm, "end": v(1019.1, -9.23) * mm});
            skLineSegment(sketch, "E400.trimOffspring", {"start": v(979.93, -9.23) * mm, "end": v(1005.33, -9.23) * mm});
            skLineSegment(sketch, "E401.trimOffspring", {"start": v(1010.65, -19.39) * mm, "end": v(1009.58, -19.39) * mm});
            skLineSegment(sketch, "E402.trimOffspring", {"start": v(1018.03, -9.23) * mm, "end": v(1019.1, -9.23) * mm});
            skLineSegment(sketch, "E403.trimOffspring", {"start": v(1048.75, -19.39) * mm, "end": v(1023.35, -19.39) * mm});
            skLineSegment(sketch, "E404.trimOffspring", {"start": v(1061.45, -19.39) * mm, "end": v(1059.02, -19.39) * mm});
            skLineSegment(sketch, "E405.trimOffspring", {"start": v(1145.85, -19.39) * mm, "end": v(1106.68, -19.39) * mm});
            skLineSegment(sketch, "E406.trimOffspring", {"start": v(1136.33, -9.23) * mm, "end": v(1189.27, -9.23) * mm});
            skLineSegment(sketch, "E407.trimOffspring", {"start": v(1136.33, -9.23) * mm, "end": v(1273.97, -9.23) * mm});
            skLineSegment(sketch, "E408.trimOffspring", {"start": v(1136.33, -9.23) * mm, "end": v(1185.36, -9.23) * mm});
            skLineSegment(sketch, "E409.trimOffspring", {"start": v(1050.57, -9.23) * mm, "end": v(1101.37, -9.23) * mm});
            skLineSegment(sketch, "E410.trimOffspring", {"start": v(1050.57, -9.23) * mm, "end": v(1102.43, -9.23) * mm});
            skLineSegment(sketch, "E411.trimOffspring", {"start": v(889.26, -18.4) * mm, "end": v(837.05, -18.4) * mm});
            skLineSegment(sketch, "E412.trimOffspring", {"start": v(879.74, -8.24) * mm, "end": v(930.55, -8.24) * mm});
            skLineSegment(sketch, "E413.trimOffspring", {"start": v(820.26, -38.6) * mm, "end": v(820.26, -38.97) * mm});
            skLineSegment(sketch, "E414.trimOffspring", {"start": v(802.43, -18.4) * mm, "end": v(763.26, -18.4) * mm});
            skLineSegment(sketch, "E415.trimOffspring", {"start": v(792.9, -8.24) * mm, "end": v(841.94, -8.24) * mm});
            skLineSegment(sketch, "E416.trimOffspring", {"start": v(792.9, -8.24) * mm, "end": v(845.84, -8.24) * mm});
            skLineSegment(sketch, "E417.trimOffspring", {"start": v(709.57, -8.24) * mm, "end": v(759, -8.24) * mm});
            skLineSegment(sketch, "E418.trimOffspring", {"start": v(622.74, -8.24) * mm, "end": v(675.67, -8.24) * mm});
            skLineSegment(sketch, "E419.trimOffspring", {"start": v(622.74, -8.24) * mm, "end": v(673.6, -8.24) * mm});
            skLineSegment(sketch, "E420.trimOffspring", {"start": v(454.39, -8.24) * mm, "end": v(503.42, -8.24) * mm});
            skLineSegment(sketch, "E421.trimOffspring", {"start": v(454.39, -8.24) * mm, "end": v(507.32, -8.24) * mm});
            skLineSegment(sketch, "E422.trimOffspring", {"start": v(454.39, -8.24) * mm, "end": v(506.26, -8.24) * mm});
            skLineSegment(sketch, "E423.trimOffspring", {"start": v(463.9, -18.4) * mm, "end": v(424.74, -18.4) * mm});
            skLineSegment(sketch, "E424.trimOffspring", {"start": v(536.97, -8.24) * mm, "end": v(588.84, -8.24) * mm});
            skLineSegment(sketch, "E425.trimOffspring", {"start": v(541.22, -8.24) * mm, "end": v(588.84, -8.24) * mm});
            skLineSegment(sketch, "E426.trimOffspring", {"start": v(545.42, -18.4) * mm, "end": v(497.8, -18.4) * mm});
            skLineSegment(sketch, "E427.trimOffspring", {"start": v(368.62, -8.24) * mm, "end": v(419.42, -8.24) * mm});
            skLineSegment(sketch, "E428", {"start": v(720.8, -14.32) * mm, "end": v(725.77, -2.44) * mm});
            skLineSegment(sketch, "E429", {"start": v(836.65, -8.24) * mm, "end": v(859.27, -8.24) * mm});
            skLineSegment(sketch, "E430", {"start": v(834.12, -11.4) * mm, "end": v(830.05, -1.66) * mm});
            skLineSegment(sketch, "E431", {"start": v(158.63, -34.93) * mm, "end": v(167.23, -55.5) * mm});
            skLineSegment(sketch, "E432", {"start": v(37.6, -16.31) * mm, "end": v(44.43, 0) * mm});
            skLineSegment(sketch, "E433", {"start": v(-643.9, -14.3) * mm, "end": v(-638.76, -2) * mm});
            skSolve(sketch);
        }
        {
            var Q0;
            {var subQ5=sQuery(id+"F2.wireOp",EDGE,"E2");Q0=makeQuery(id+"F2.imprint","IMPRINT",FACE,{"disambiguationData":[TD([[makeQuery(id+"F2.imprint","IMPRINT",EDGE,{"derivedFrom":subQ5}),1.0]])]});}
            var Q1;
            {var subQ4=sQuery(id+"F2.wireOp",EDGE,"E55.trimOffspring");Q1=makeQuery(id+"F2.imprint","IMPRINT",FACE,{"disambiguationData":[TD([[makeQuery(id+"F2.imprint","IMPRINT",EDGE,{"derivedFrom":subQ4}),-1.0]])]});}
            var Q2;
            {var subQ0=sQuery(id+"F2.wireOp",EDGE,"E57.trimOffspring");Q2=makeQuery(id+"F2.imprint","IMPRINT",FACE,{"disambiguationData":[TD([[makeQuery(id+"F2.imprint","IMPRINT",EDGE,{"derivedFrom":subQ0}),-1.0]])]});}
            var Q3;
            {var subQ0=sQuery(id+"F2.wireOp",EDGE,"E21");var subQ1=sQuery(id+"F2.wireOp",EDGE,"E20");var subQ2=makeQuery(id+"F2.imprint","INTERSECT",VERTEX,{"derivedFrom":[subQ1,subQ0]});Q3=makeQuery(id+"F2.imprint","IMPRINT",FACE,{"disambiguationData":[TD([[makeQuery(id+"F2.imprint","IMPRINT",EDGE,{"disambiguationData":[TD([[subQ2,-1.0]])],"derivedFrom":subQ1}),1.0]])]});}
            var Q4;
            {var subQ0=sQuery(id+"F2.wireOp",EDGE,"E60.trimOffspring");var subQ3=makeQuery(id+"F2.imprint","IMPRINT",VERTEX,{"derivedFrom":subQ0});Q4=makeQuery(id+"F2.imprint","IMPRINT",FACE,{"disambiguationData":[TD([[makeQuery(id+"F2.imprint","IMPRINT",EDGE,{"disambiguationData":[TD([[subQ3,1.0]])],"derivedFrom":subQ0}),-1.0]])]});}
            var Q5;
            {var subQ5=sQuery(id+"F2.wireOp",EDGE,"E28");Q5=makeQuery(id+"F2.imprint","IMPRINT",FACE,{"disambiguationData":[TD([[makeQuery(id+"F2.imprint","IMPRINT",EDGE,{"derivedFrom":subQ5}),1.0]])]});}
            var Q6;
            {var subQ0=sQuery(id+"F2.wireOp",EDGE,"E46");var subQ1=sQuery(id+"F2.wireOp",EDGE,"E35");var subQ2=makeQuery(id+"F2.imprint","INTERSECT",VERTEX,{"derivedFrom":[subQ1,subQ0]});Q6=makeQuery(id+"F2.imprint","IMPRINT",FACE,{"disambiguationData":[TD([[makeQuery(id+"F2.imprint","IMPRINT",EDGE,{"disambiguationData":[TD([[subQ2,1.0]])],"derivedFrom":subQ1}),1.0]])]});}
            var Q7;
            {var subQ0=sQuery(id+"F2.wireOp",EDGE,"E45");var subQ3=makeQuery(id+"F2.imprint","IMPRINT",VERTEX,{"disambiguationData":[OD(1.0)],"derivedFrom":subQ0});Q7=makeQuery(id+"F2.imprint","IMPRINT",FACE,{"disambiguationData":[TD([[makeQuery(id+"F2.imprint","IMPRINT",EDGE,{"disambiguationData":[TD([[subQ3,1.0]])],"derivedFrom":subQ0}),-1.0]])]});}
            var Q8;
            {var subQ0=sQuery(id+"F2.wireOp",EDGE,"E41");var subQ1=sQuery(id+"F2.wireOp",EDGE,"E40");var subQ2=makeQuery(id+"F2.imprint","INTERSECT",VERTEX,{"derivedFrom":[subQ1,subQ0]});Q8=makeQuery(id+"F2.imprint","IMPRINT",FACE,{"disambiguationData":[TD([[makeQuery(id+"F2.imprint","IMPRINT",EDGE,{"disambiguationData":[TD([[subQ2,-1.0]])],"derivedFrom":subQ1}),1.0]])]});}
            var Q9;
            {var subQ0=sQuery(id+"F2.wireOp",EDGE,"E59.trimOffspring");var subQ1=sQuery(id+"F2.wireOp",EDGE,"E41");var subQ2=makeQuery(id+"F2.imprint","INTERSECT",VERTEX,{"derivedFrom":[subQ1,subQ0]});Q9=makeQuery(id+"F2.imprint","IMPRINT",FACE,{"disambiguationData":[TD([[makeQuery(id+"F2.imprint","IMPRINT",EDGE,{"disambiguationData":[TD([[subQ2,-1.0]])],"derivedFrom":subQ1}),1.0]])]});}
            var Q10;
            {var subQ0=sQuery(id+"F2.wireOp",EDGE,"E59.trimOffspring");var subQ1=sQuery(id+"F2.wireOp",EDGE,"E42");var subQ2=makeQuery(id+"F2.imprint","INTERSECT",VERTEX,{"derivedFrom":[subQ1,subQ0]});Q10=makeQuery(id+"F2.imprint","IMPRINT",FACE,{"disambiguationData":[TD([[makeQuery(id+"F2.imprint","IMPRINT",EDGE,{"disambiguationData":[TD([[subQ2,-1.0]])],"derivedFrom":subQ1}),-1.0]])]});}
            var Q11;
            {var subQ0=sQuery(id+"F2.wireOp",EDGE,"E42");var subQ1=sQuery(id+"F2.wireOp",EDGE,"E40");var subQ2=makeQuery(id+"F2.imprint","INTERSECT",VERTEX,{"derivedFrom":[subQ1,subQ0]});Q11=makeQuery(id+"F2.imprint","IMPRINT",FACE,{"disambiguationData":[TD([[makeQuery(id+"F2.imprint","IMPRINT",EDGE,{"disambiguationData":[TD([[subQ2,1.0]])],"derivedFrom":subQ1}),1.0]])]});}
            var Q12;
            {var subQ0=sQuery(id+"F2.wireOp",EDGE,"E47");var subQ1=sQuery(id+"F2.wireOp",EDGE,"E46");var subQ2=makeQuery(id+"F2.imprint","INTERSECT",VERTEX,{"derivedFrom":[subQ1,subQ0]});Q12=makeQuery(id+"F2.imprint","IMPRINT",FACE,{"disambiguationData":[TD([[makeQuery(id+"F2.imprint","IMPRINT",EDGE,{"disambiguationData":[TD([[subQ2,-1.0]])],"derivedFrom":subQ1}),1.0]])]});}
            var Q13;
            {var subQ1=sQuery(id+"F2.wireOp",EDGE,"E45");var subQ8=makeQuery(id+"F2.imprint","IMPRINT",VERTEX,{"disambiguationData":[OD(0.0)],"derivedFrom":subQ1});Q13=makeQuery(id+"F2.imprint","IMPRINT",FACE,{"disambiguationData":[TD([[makeQuery(id+"F2.imprint","IMPRINT",EDGE,{"disambiguationData":[TD([[subQ8,1.0]])],"derivedFrom":subQ1}),-1.0]])]});}
            var Q14;
            {var subQ6=sQuery(id+"F2.wireOp",EDGE,"E63");Q14=makeQuery(id+"F2.imprint","IMPRINT",FACE,{"disambiguationData":[TD([[makeQuery(id+"F2.imprint","IMPRINT",EDGE,{"derivedFrom":subQ6}),1.0]])]});}
            var Q15;
            {var subQ1=sQuery(id+"F2.wireOp",EDGE,"E45");var subQ3=sQuery(id+"F2.wireOp",EDGE,"E64");var subQ4=makeQuery(id+"F2.imprint","INTERSECT",VERTEX,{"derivedFrom":[subQ1,subQ3]});Q15=makeQuery(id+"F2.imprint","IMPRINT",FACE,{"disambiguationData":[TD([[makeQuery(id+"F2.imprint","IMPRINT",EDGE,{"disambiguationData":[TD([[subQ4,1.0]])],"derivedFrom":subQ1}),-1.0]])]});}
            var Q16;
            {var subQ0=sQuery(id+"F2.wireOp",EDGE,"E111.trimOffspring");var subQ5=makeQuery(id+"F2.imprint","IMPRINT",VERTEX,{"derivedFrom":subQ0});Q16=makeQuery(id+"F2.imprint","IMPRINT",FACE,{"disambiguationData":[TD([[makeQuery(id+"F2.imprint","IMPRINT",EDGE,{"disambiguationData":[TD([[subQ5,1.0]])],"derivedFrom":subQ0}),-1.0]])]});}
            var Q17;
            {var subQ3=sQuery(id+"F2.wireOp",EDGE,"E56.trimOffspring");var subQ5=sQuery(id+"F2.wireOp",EDGE,"E39");var subQ6=makeQuery(id+"F2.imprint","INTERSECT",VERTEX,{"derivedFrom":[subQ5,subQ3]});Q17=makeQuery(id+"F2.imprint","IMPRINT",FACE,{"disambiguationData":[TD([[makeQuery(id+"F2.imprint","IMPRINT",EDGE,{"disambiguationData":[TD([[subQ6,-1.0]])],"derivedFrom":subQ5}),1.0]])]});}
            var Q18;
            {var subQ0=sQuery(id+"F2.wireOp",EDGE,"E113.trimOffspring");Q18=makeQuery(id+"F2.imprint","IMPRINT",FACE,{"disambiguationData":[TD([[makeQuery(id+"F2.imprint","IMPRINT",EDGE,{"derivedFrom":subQ0}),-1.0]])]});}
            var Q19;
            {var subQ0=sQuery(id+"F2.wireOp",EDGE,"E82");var subQ1=sQuery(id+"F2.wireOp",EDGE,"E81");var subQ2=makeQuery(id+"F2.imprint","INTERSECT",VERTEX,{"derivedFrom":[subQ1,subQ0]});Q19=makeQuery(id+"F2.imprint","IMPRINT",FACE,{"disambiguationData":[TD([[makeQuery(id+"F2.imprint","IMPRINT",EDGE,{"disambiguationData":[TD([[subQ2,-1.0]])],"derivedFrom":subQ1}),1.0]])]});}
            var Q20;
            {var subQ0=sQuery(id+"F2.wireOp",EDGE,"E116.trimOffspring");var subQ3=makeQuery(id+"F2.imprint","IMPRINT",VERTEX,{"derivedFrom":subQ0});Q20=makeQuery(id+"F2.imprint","IMPRINT",FACE,{"disambiguationData":[TD([[makeQuery(id+"F2.imprint","IMPRINT",EDGE,{"disambiguationData":[TD([[subQ3,1.0]])],"derivedFrom":subQ0}),-1.0]])]});}
            var Q21;
            {var subQ3=sQuery(id+"F2.wireOp",EDGE,"E115.trimOffspring");var subQ5=makeQuery(id+"F2.imprint","IMPRINT",VERTEX,{"derivedFrom":subQ3});Q21=makeQuery(id+"F2.imprint","IMPRINT",FACE,{"disambiguationData":[TD([[makeQuery(id+"F2.imprint","IMPRINT",EDGE,{"disambiguationData":[TD([[subQ5,1.0]])],"derivedFrom":subQ3}),1.0]])]});}
            var Q22;
            {var subQ0=sQuery(id+"F2.wireOp",EDGE,"E101");var subQ3=makeQuery(id+"F2.imprint","IMPRINT",VERTEX,{"disambiguationData":[OD(1.0)],"derivedFrom":subQ0});Q22=makeQuery(id+"F2.imprint","IMPRINT",FACE,{"disambiguationData":[TD([[makeQuery(id+"F2.imprint","IMPRINT",EDGE,{"disambiguationData":[TD([[subQ3,1.0]])],"derivedFrom":subQ0}),-1.0]])]});}
            var Q23;
            {var subQ0=sQuery(id+"F2.wireOp",EDGE,"E97");var subQ1=sQuery(id+"F2.wireOp",EDGE,"E75");var subQ2=makeQuery(id+"F2.imprint","INTERSECT",VERTEX,{"derivedFrom":[subQ1,subQ0]});Q23=makeQuery(id+"F2.imprint","IMPRINT",FACE,{"disambiguationData":[TD([[makeQuery(id+"F2.imprint","IMPRINT",EDGE,{"disambiguationData":[TD([[subQ2,-1.0]])],"derivedFrom":subQ1}),1.0]])]});}
            var Q24;
            {var subQ0=sQuery(id+"F2.wireOp",EDGE,"E115.trimOffspring");var subQ1=sQuery(id+"F2.wireOp",EDGE,"E97");var subQ2=makeQuery(id+"F2.imprint","INTERSECT",VERTEX,{"derivedFrom":[subQ1,subQ0]});Q24=makeQuery(id+"F2.imprint","IMPRINT",FACE,{"disambiguationData":[TD([[makeQuery(id+"F2.imprint","IMPRINT",EDGE,{"disambiguationData":[TD([[subQ2,-1.0]])],"derivedFrom":subQ1}),1.0]])]});}
            var Q25;
            {var subQ0=sQuery(id+"F2.wireOp",EDGE,"E115.trimOffspring");var subQ1=sQuery(id+"F2.wireOp",EDGE,"E98");var subQ2=makeQuery(id+"F2.imprint","INTERSECT",VERTEX,{"derivedFrom":[subQ1,subQ0]});Q25=makeQuery(id+"F2.imprint","IMPRINT",FACE,{"disambiguationData":[TD([[makeQuery(id+"F2.imprint","IMPRINT",EDGE,{"disambiguationData":[TD([[subQ2,-1.0]])],"derivedFrom":subQ1}),-1.0]])]});}
            var Q26;
            {var subQ0=sQuery(id+"F2.wireOp",EDGE,"E98");var subQ1=sQuery(id+"F2.wireOp",EDGE,"E75");var subQ2=makeQuery(id+"F2.imprint","INTERSECT",VERTEX,{"derivedFrom":[subQ1,subQ0]});Q26=makeQuery(id+"F2.imprint","IMPRINT",FACE,{"disambiguationData":[TD([[makeQuery(id+"F2.imprint","IMPRINT",EDGE,{"disambiguationData":[TD([[subQ2,1.0]])],"derivedFrom":subQ1}),1.0]])]});}
            var Q27;
            {var subQ0=sQuery(id+"F2.wireOp",EDGE,"E103");var subQ1=sQuery(id+"F2.wireOp",EDGE,"E102");var subQ2=makeQuery(id+"F2.imprint","INTERSECT",VERTEX,{"derivedFrom":[subQ1,subQ0]});Q27=makeQuery(id+"F2.imprint","IMPRINT",FACE,{"disambiguationData":[TD([[makeQuery(id+"F2.imprint","IMPRINT",EDGE,{"disambiguationData":[TD([[subQ2,-1.0]])],"derivedFrom":subQ1}),1.0]])]});}
            var Q28;
            {var subQ1=sQuery(id+"F2.wireOp",EDGE,"E101");var subQ8=makeQuery(id+"F2.imprint","IMPRINT",VERTEX,{"disambiguationData":[OD(0.0)],"derivedFrom":subQ1});Q28=makeQuery(id+"F2.imprint","IMPRINT",FACE,{"disambiguationData":[TD([[makeQuery(id+"F2.imprint","IMPRINT",EDGE,{"disambiguationData":[TD([[subQ8,1.0]])],"derivedFrom":subQ1}),-1.0]])]});}
            var Q29;
            {var subQ3=sQuery(id+"F2.wireOp",EDGE,"E171.trimOffspring");Q29=makeQuery(id+"F2.imprint","IMPRINT",FACE,{"disambiguationData":[TD([[makeQuery(id+"F2.imprint","IMPRINT",EDGE,{"derivedFrom":subQ3}),-1.0]])]});}
            var Q30;
            {var subQ7=sQuery(id+"F2.wireOp",EDGE,"E119");Q30=makeQuery(id+"F2.imprint","IMPRINT",FACE,{"disambiguationData":[TD([[makeQuery(id+"F2.imprint","IMPRINT",EDGE,{"derivedFrom":subQ7}),1.0]])]});}
            var Q31;
            {var subQ0=sQuery(id+"F2.wireOp",EDGE,"E120");var subQ1=sQuery(id+"F2.wireOp",EDGE,"E101");var subQ2=makeQuery(id+"F2.imprint","INTERSECT",VERTEX,{"derivedFrom":[subQ1,subQ0]});Q31=makeQuery(id+"F2.imprint","IMPRINT",FACE,{"disambiguationData":[TD([[makeQuery(id+"F2.imprint","IMPRINT",EDGE,{"disambiguationData":[TD([[subQ2,1.0]])],"derivedFrom":subQ1}),-1.0]])]});}
            var Q32;
            {var subQ0=sQuery(id+"F2.wireOp",EDGE,"E173.trimOffspring");Q32=makeQuery(id+"F2.imprint","IMPRINT",FACE,{"disambiguationData":[TD([[makeQuery(id+"F2.imprint","IMPRINT",EDGE,{"derivedFrom":subQ0}),-1.0]])]});}
            var Q33;
            {var subQ0=sQuery(id+"F2.wireOp",EDGE,"E176.trimOffspring");var subQ3=makeQuery(id+"F2.imprint","IMPRINT",VERTEX,{"derivedFrom":subQ0});Q33=makeQuery(id+"F2.imprint","IMPRINT",FACE,{"disambiguationData":[TD([[makeQuery(id+"F2.imprint","IMPRINT",EDGE,{"disambiguationData":[TD([[subQ3,1.0]])],"derivedFrom":subQ0}),-1.0]])]});}
            var Q34;
            {var subQ0=sQuery(id+"F2.wireOp",EDGE,"E138");var subQ1=sQuery(id+"F2.wireOp",EDGE,"E137");var subQ2=makeQuery(id+"F2.imprint","INTERSECT",VERTEX,{"derivedFrom":[subQ1,subQ0]});Q34=makeQuery(id+"F2.imprint","IMPRINT",FACE,{"disambiguationData":[TD([[makeQuery(id+"F2.imprint","IMPRINT",EDGE,{"disambiguationData":[TD([[subQ2,-1.0]])],"derivedFrom":subQ1}),1.0]])]});}
            var Q35;
            {var subQ5=sQuery(id+"F2.wireOp",EDGE,"E144");Q35=makeQuery(id+"F2.imprint","IMPRINT",FACE,{"disambiguationData":[TD([[makeQuery(id+"F2.imprint","IMPRINT",EDGE,{"derivedFrom":subQ5}),1.0]])]});}
            var Q36;
            {var subQ0=sQuery(id+"F2.wireOp",EDGE,"E161");var subQ3=makeQuery(id+"F2.imprint","IMPRINT",VERTEX,{"disambiguationData":[OD(1.0)],"derivedFrom":subQ0});Q36=makeQuery(id+"F2.imprint","IMPRINT",FACE,{"disambiguationData":[TD([[makeQuery(id+"F2.imprint","IMPRINT",EDGE,{"disambiguationData":[TD([[subQ3,1.0]])],"derivedFrom":subQ0}),-1.0]])]});}
            var Q37;
            {var subQ0=sQuery(id+"F2.wireOp",EDGE,"E162");var subQ1=sQuery(id+"F2.wireOp",EDGE,"E151");var subQ2=makeQuery(id+"F2.imprint","INTERSECT",VERTEX,{"derivedFrom":[subQ1,subQ0]});Q37=makeQuery(id+"F2.imprint","IMPRINT",FACE,{"disambiguationData":[TD([[makeQuery(id+"F2.imprint","IMPRINT",EDGE,{"disambiguationData":[TD([[subQ2,1.0]])],"derivedFrom":subQ1}),1.0]])]});}
            var Q38;
            {var subQ0=sQuery(id+"F2.wireOp",EDGE,"E157");var subQ1=sQuery(id+"F2.wireOp",EDGE,"E156");var subQ2=makeQuery(id+"F2.imprint","INTERSECT",VERTEX,{"derivedFrom":[subQ1,subQ0]});Q38=makeQuery(id+"F2.imprint","IMPRINT",FACE,{"disambiguationData":[TD([[makeQuery(id+"F2.imprint","IMPRINT",EDGE,{"disambiguationData":[TD([[subQ2,-1.0]])],"derivedFrom":subQ1}),1.0]])]});}
            var Q39;
            {var subQ0=sQuery(id+"F2.wireOp",EDGE,"E175.trimOffspring");var subQ1=sQuery(id+"F2.wireOp",EDGE,"E157");var subQ2=makeQuery(id+"F2.imprint","INTERSECT",VERTEX,{"derivedFrom":[subQ1,subQ0]});Q39=makeQuery(id+"F2.imprint","IMPRINT",FACE,{"disambiguationData":[TD([[makeQuery(id+"F2.imprint","IMPRINT",EDGE,{"disambiguationData":[TD([[subQ2,-1.0]])],"derivedFrom":subQ1}),1.0]])]});}
            var Q40;
            {var subQ0=sQuery(id+"F2.wireOp",EDGE,"E175.trimOffspring");var subQ1=sQuery(id+"F2.wireOp",EDGE,"E158");var subQ2=makeQuery(id+"F2.imprint","INTERSECT",VERTEX,{"derivedFrom":[subQ1,subQ0]});Q40=makeQuery(id+"F2.imprint","IMPRINT",FACE,{"disambiguationData":[TD([[makeQuery(id+"F2.imprint","IMPRINT",EDGE,{"disambiguationData":[TD([[subQ2,-1.0]])],"derivedFrom":subQ1}),-1.0]])]});}
            var Q41;
            {var subQ0=sQuery(id+"F2.wireOp",EDGE,"E158");var subQ1=sQuery(id+"F2.wireOp",EDGE,"E156");var subQ2=makeQuery(id+"F2.imprint","INTERSECT",VERTEX,{"derivedFrom":[subQ1,subQ0]});Q41=makeQuery(id+"F2.imprint","IMPRINT",FACE,{"disambiguationData":[TD([[makeQuery(id+"F2.imprint","IMPRINT",EDGE,{"disambiguationData":[TD([[subQ2,1.0]])],"derivedFrom":subQ1}),1.0]])]});}
            var Q42;
            {var subQ0=sQuery(id+"F2.wireOp",EDGE,"E163");var subQ1=sQuery(id+"F2.wireOp",EDGE,"E162");var subQ2=makeQuery(id+"F2.imprint","INTERSECT",VERTEX,{"derivedFrom":[subQ1,subQ0]});Q42=makeQuery(id+"F2.imprint","IMPRINT",FACE,{"disambiguationData":[TD([[makeQuery(id+"F2.imprint","IMPRINT",EDGE,{"disambiguationData":[TD([[subQ2,-1.0]])],"derivedFrom":subQ1}),1.0]])]});}
            var Q43;
            {var subQ1=sQuery(id+"F2.wireOp",EDGE,"E161");var subQ8=makeQuery(id+"F2.imprint","IMPRINT",VERTEX,{"disambiguationData":[OD(0.0)],"derivedFrom":subQ1});Q43=makeQuery(id+"F2.imprint","IMPRINT",FACE,{"disambiguationData":[TD([[makeQuery(id+"F2.imprint","IMPRINT",EDGE,{"disambiguationData":[TD([[subQ8,1.0]])],"derivedFrom":subQ1}),-1.0]])]});}
            var Q44;
            {var subQ6=sQuery(id+"F2.wireOp",EDGE,"E179");Q44=makeQuery(id+"F2.imprint","IMPRINT",FACE,{"disambiguationData":[TD([[makeQuery(id+"F2.imprint","IMPRINT",EDGE,{"derivedFrom":subQ6}),1.0]])]});}
            var Q45;
            {var subQ1=sQuery(id+"F2.wireOp",EDGE,"E161");var subQ3=sQuery(id+"F2.wireOp",EDGE,"E180");var subQ4=makeQuery(id+"F2.imprint","INTERSECT",VERTEX,{"derivedFrom":[subQ1,subQ3]});Q45=makeQuery(id+"F2.imprint","IMPRINT",FACE,{"disambiguationData":[TD([[makeQuery(id+"F2.imprint","IMPRINT",EDGE,{"disambiguationData":[TD([[subQ4,1.0]])],"derivedFrom":subQ1}),-1.0]])]});}
            var Q46;
            {var subQ0=sQuery(id+"F2.wireOp",EDGE,"E227.trimOffspring");var subQ10=makeQuery(id+"F2.imprint","IMPRINT",VERTEX,{"derivedFrom":subQ0});Q46=makeQuery(id+"F2.imprint","IMPRINT",FACE,{"disambiguationData":[TD([[makeQuery(id+"F2.imprint","IMPRINT",EDGE,{"disambiguationData":[TD([[subQ10,1.0]])],"derivedFrom":subQ0}),-1.0]])]});}
            var Q47;
            {var subQ3=sQuery(id+"F2.wireOp",EDGE,"E172.trimOffspring");var subQ5=sQuery(id+"F2.wireOp",EDGE,"E155");var subQ6=makeQuery(id+"F2.imprint","INTERSECT",VERTEX,{"derivedFrom":[subQ5,subQ3]});Q47=makeQuery(id+"F2.imprint","IMPRINT",FACE,{"disambiguationData":[TD([[makeQuery(id+"F2.imprint","IMPRINT",EDGE,{"disambiguationData":[TD([[subQ6,-1.0]])],"derivedFrom":subQ5}),1.0]])]});}
            var Q48;
            {var subQ4=sQuery(id+"F2.wireOp",EDGE,"E229.trimOffspring");Q48=makeQuery(id+"F2.imprint","IMPRINT",FACE,{"disambiguationData":[TD([[makeQuery(id+"F2.imprint","IMPRINT",EDGE,{"derivedFrom":subQ4}),-1.0]])]});}
            extrude(context, id + "F3", {"entities" : qUnion([Q0, Q1, Q2, Q3, Q4, Q5, Q6, Q7, Q8, Q9, Q10, Q11, Q12, Q13, Q14, Q15, Q16, Q17, Q18, Q19, Q20, Q21, Q22, Q23, Q24, Q25, Q26, Q27, Q28, Q29, Q30, Q31, Q32, Q33, Q34, Q35, Q36, Q37, Q38, Q39, Q40, Q41, Q42, Q43, Q44, Q45, Q46, Q47, Q48]), "operationType" : NewBodyOperationType.REMOVE, "depth" : 254 * mm, "offsetDistance" : 25.4 * mm, "hasSecondDirection" : true, "secondDirectionOppositeDirection" : true, "secondDirectionDepth" : 254 * mm});
        }
        {
            var Q0;
            {var subQ0=sQuery(id+"F2.wireOp",EDGE,"E198");var subQ1=sQuery(id+"F2.wireOp",EDGE,"E197");var subQ2=makeQuery(id+"F2.imprint","INTERSECT",VERTEX,{"derivedFrom":[subQ1,subQ0]});Q0=makeQuery(id+"F2.imprint","IMPRINT",FACE,{"disambiguationData":[TD([[makeQuery(id+"F2.imprint","IMPRINT",EDGE,{"disambiguationData":[TD([[subQ2,-1.0]])],"derivedFrom":subQ1}),1.0]])]});}
            var Q1;
            {var subQ5=sQuery(id+"F2.wireOp",EDGE,"E232.trimOffspring");var subQ7=makeQuery(id+"F2.imprint","IMPRINT",VERTEX,{"derivedFrom":subQ5});Q1=makeQuery(id+"F2.imprint","IMPRINT",FACE,{"disambiguationData":[TD([[makeQuery(id+"F2.imprint","IMPRINT",EDGE,{"disambiguationData":[TD([[subQ7,1.0]])],"derivedFrom":subQ5}),-1.0]])]});}
            var Q2;
            {var subQ0=sQuery(id+"F2.wireOp",EDGE,"E231.trimOffspring");var subQ1=makeQuery(id+"F2.imprint","IMPRINT",VERTEX,{"derivedFrom":subQ0});Q2=makeQuery(id+"F2.imprint","IMPRINT",FACE,{"disambiguationData":[TD([[makeQuery(id+"F2.imprint","IMPRINT",EDGE,{"disambiguationData":[TD([[subQ1,1.0]])],"derivedFrom":subQ0}),1.0]])]});}
            var Q3;
            {var subQ0=sQuery(id+"F2.wireOp",EDGE,"E217");var subQ3=makeQuery(id+"F2.imprint","IMPRINT",VERTEX,{"derivedFrom":subQ0});Q3=makeQuery(id+"F2.imprint","IMPRINT",FACE,{"disambiguationData":[TD([[makeQuery(id+"F2.imprint","IMPRINT",EDGE,{"disambiguationData":[TD([[subQ3,1.0]])],"derivedFrom":subQ0}),-1.0]])]});}
            var Q4;
            {var subQ0=sQuery(id+"F2.wireOp",EDGE,"E217");var subQ1=sQuery(id+"F2.wireOp",EDGE,"E214");var subQ2=makeQuery(id+"F2.imprint","INTERSECT",VERTEX,{"derivedFrom":[subQ1,subQ0]});Q4=makeQuery(id+"F2.imprint","IMPRINT",FACE,{"disambiguationData":[TD([[makeQuery(id+"F2.imprint","IMPRINT",EDGE,{"disambiguationData":[TD([[subQ2,1.0]])],"derivedFrom":subQ1}),-1.0]])]});}
            var Q5;
            {var subQ0=sQuery(id+"F2.wireOp",EDGE,"E231.trimOffspring");var subQ1=sQuery(id+"F2.wireOp",EDGE,"E213");var subQ2=makeQuery(id+"F2.imprint","INTERSECT",VERTEX,{"derivedFrom":[subQ1,subQ0]});Q5=makeQuery(id+"F2.imprint","IMPRINT",FACE,{"disambiguationData":[TD([[makeQuery(id+"F2.imprint","IMPRINT",EDGE,{"disambiguationData":[TD([[subQ2,-1.0]])],"derivedFrom":subQ1}),1.0]])]});}
            var Q6;
            {var subQ0=sQuery(id+"F2.wireOp",EDGE,"E219");var subQ1=sQuery(id+"F2.wireOp",EDGE,"E218");var subQ2=makeQuery(id+"F2.imprint","INTERSECT",VERTEX,{"derivedFrom":[subQ1,subQ0]});Q6=makeQuery(id+"F2.imprint","IMPRINT",FACE,{"disambiguationData":[TD([[makeQuery(id+"F2.imprint","IMPRINT",EDGE,{"disambiguationData":[TD([[subQ2,-1.0]])],"derivedFrom":subQ1}),1.0]])]});}
            var Q7;
            {var subQ0=sQuery(id+"F2.wireOp",EDGE,"E219");var subQ1=sQuery(id+"F2.wireOp",EDGE,"E217");var subQ2=makeQuery(id+"F2.imprint","INTERSECT",VERTEX,{"derivedFrom":[subQ1,subQ0]});Q7=makeQuery(id+"F2.imprint","IMPRINT",FACE,{"disambiguationData":[TD([[makeQuery(id+"F2.imprint","IMPRINT",EDGE,{"disambiguationData":[TD([[subQ2,-1.0]])],"derivedFrom":subQ1}),-1.0]])]});}
            var Q8;
            {var subQ1=sQuery(id+"F2.wireOp",EDGE,"E235");Q8=makeQuery(id+"F2.imprint","IMPRINT",FACE,{"disambiguationData":[TD([[makeQuery(id+"F2.imprint","IMPRINT",EDGE,{"derivedFrom":subQ1}),1.0]])]});}
            var Q9;
            {var subQ0=sQuery(id+"F2.wireOp",EDGE,"E237");var subQ1=makeQuery(id+"F2.imprint","IMPRINT",VERTEX,{"derivedFrom":subQ0});Q9=makeQuery(id+"F2.imprint","IMPRINT",FACE,{"disambiguationData":[TD([[makeQuery(id+"F2.imprint","IMPRINT",EDGE,{"disambiguationData":[TD([[subQ1,1.0]])],"derivedFrom":subQ0}),-1.0]])]});}
            var Q10;
            {var subQ3=sQuery(id+"F2.wireOp",EDGE,"E286.trimOffspring");Q10=makeQuery(id+"F2.imprint","IMPRINT",FACE,{"disambiguationData":[TD([[makeQuery(id+"F2.imprint","IMPRINT",EDGE,{"derivedFrom":subQ3}),-1.0]])]});}
            var Q11;
            {var subQ0=sQuery(id+"F2.wireOp",EDGE,"E288.trimOffspring");Q11=makeQuery(id+"F2.imprint","IMPRINT",FACE,{"disambiguationData":[TD([[makeQuery(id+"F2.imprint","IMPRINT",EDGE,{"derivedFrom":subQ0}),-1.0]])]});}
            var Q12;
            {var subQ1=sQuery(id+"F2.wireOp",EDGE,"E253");var subQ5=sQuery(id+"F2.wireOp",EDGE,"E254");var subQ6=makeQuery(id+"F2.imprint","INTERSECT",VERTEX,{"derivedFrom":[subQ1,subQ5]});Q12=makeQuery(id+"F2.imprint","IMPRINT",FACE,{"disambiguationData":[TD([[makeQuery(id+"F2.imprint","IMPRINT",EDGE,{"disambiguationData":[TD([[subQ6,-1.0]])],"derivedFrom":subQ1}),1.0]])]});}
            var Q13;
            {var subQ0=sQuery(id+"F2.wireOp",EDGE,"E291.trimOffspring");var subQ3=makeQuery(id+"F2.imprint","IMPRINT",VERTEX,{"derivedFrom":subQ0});Q13=makeQuery(id+"F2.imprint","IMPRINT",FACE,{"disambiguationData":[TD([[makeQuery(id+"F2.imprint","IMPRINT",EDGE,{"disambiguationData":[TD([[subQ3,1.0]])],"derivedFrom":subQ0}),-1.0]])]});}
            var Q14;
            {var subQ5=sQuery(id+"F2.wireOp",EDGE,"E260");Q14=makeQuery(id+"F2.imprint","IMPRINT",FACE,{"disambiguationData":[TD([[makeQuery(id+"F2.imprint","IMPRINT",EDGE,{"derivedFrom":subQ5}),1.0]])]});}
            var Q15;
            {var subQ4=sQuery(id+"F2.wireOp",EDGE,"E423.trimOffspring");var subQ10=makeQuery(id+"F2.imprint","IMPRINT",VERTEX,{"derivedFrom":subQ4});Q15=makeQuery(id+"F2.imprint","IMPRINT",FACE,{"disambiguationData":[TD([[makeQuery(id+"F2.imprint","IMPRINT",EDGE,{"disambiguationData":[TD([[subQ10,1.0]])],"derivedFrom":subQ4}),-1.0]])]});}
            var Q16;
            {var subQ4=sQuery(id+"F2.wireOp",EDGE,"E273");var subQ5=sQuery(id+"F2.wireOp",EDGE,"E272");var subQ6=makeQuery(id+"F2.imprint","INTERSECT",VERTEX,{"derivedFrom":[subQ5,subQ4]});Q16=makeQuery(id+"F2.imprint","IMPRINT",FACE,{"disambiguationData":[TD([[makeQuery(id+"F2.imprint","IMPRINT",EDGE,{"disambiguationData":[TD([[subQ6,-1.0]])],"derivedFrom":subQ5}),1.0]])]});}
            var Q17;
            {var subQ4=sQuery(id+"F2.wireOp",EDGE,"E426.trimOffspring");var subQ8=makeQuery(id+"F2.imprint","IMPRINT",VERTEX,{"derivedFrom":subQ4});Q17=makeQuery(id+"F2.imprint","IMPRINT",FACE,{"disambiguationData":[TD([[makeQuery(id+"F2.imprint","IMPRINT",EDGE,{"disambiguationData":[TD([[subQ8,1.0]])],"derivedFrom":subQ4}),-1.0]])]});}
            var Q18;
            {var subQ5=sQuery(id+"F2.wireOp",EDGE,"E294");Q18=makeQuery(id+"F2.imprint","IMPRINT",FACE,{"disambiguationData":[TD([[makeQuery(id+"F2.imprint","IMPRINT",EDGE,{"derivedFrom":subQ5}),1.0]])]});}
            var Q19;
            {var subQ4=sQuery(id+"F2.wireOp",EDGE,"E341.trimOffspring");var subQ10=makeQuery(id+"F2.imprint","IMPRINT",VERTEX,{"derivedFrom":subQ4});Q19=makeQuery(id+"F2.imprint","IMPRINT",FACE,{"disambiguationData":[TD([[makeQuery(id+"F2.imprint","IMPRINT",EDGE,{"disambiguationData":[TD([[subQ10,1.0]])],"derivedFrom":subQ4}),-1.0]])]});}
            var Q20;
            {var subQ4=sQuery(id+"F2.wireOp",EDGE,"E346.trimOffspring");var subQ9=makeQuery(id+"F2.imprint","IMPRINT",VERTEX,{"derivedFrom":subQ4});Q20=makeQuery(id+"F2.imprint","IMPRINT",FACE,{"disambiguationData":[TD([[makeQuery(id+"F2.imprint","IMPRINT",EDGE,{"disambiguationData":[TD([[subQ9,1.0]])],"derivedFrom":subQ4}),-1.0]])]});}
            var Q21;
            {var subQ4=sQuery(id+"F2.wireOp",EDGE,"E307");var subQ7=makeQuery(id+"F2.imprint","IMPRINT",VERTEX,{"derivedFrom":subQ4});Q21=makeQuery(id+"F2.imprint","IMPRINT",FACE,{"disambiguationData":[TD([[makeQuery(id+"F2.imprint","IMPRINT",EDGE,{"disambiguationData":[TD([[subQ7,1.0]])],"derivedFrom":subQ4}),1.0]])]});}
            var Q22;
            {var subQ4=sQuery(id+"F2.wireOp",EDGE,"E414.trimOffspring");var subQ10=makeQuery(id+"F2.imprint","IMPRINT",VERTEX,{"derivedFrom":subQ4});Q22=makeQuery(id+"F2.imprint","IMPRINT",FACE,{"disambiguationData":[TD([[makeQuery(id+"F2.imprint","IMPRINT",EDGE,{"disambiguationData":[TD([[subQ10,1.0]])],"derivedFrom":subQ4}),-1.0]])]});}
            var Q23;
            {var subQ0=sQuery(id+"F2.wireOp",EDGE,"E334");var subQ3=makeQuery(id+"F2.imprint","IMPRINT",VERTEX,{"derivedFrom":subQ0});Q23=makeQuery(id+"F2.imprint","IMPRINT",FACE,{"disambiguationData":[TD([[makeQuery(id+"F2.imprint","IMPRINT",EDGE,{"disambiguationData":[TD([[subQ3,1.0]])],"derivedFrom":subQ0}),1.0]])]});}
            var Q24;
            {var subQ4=sQuery(id+"F2.wireOp",EDGE,"E349");Q24=makeQuery(id+"F2.imprint","IMPRINT",FACE,{"disambiguationData":[TD([[makeQuery(id+"F2.imprint","IMPRINT",EDGE,{"derivedFrom":subQ4}),1.0]])]});}
            var Q25;
            {var subQ3=sQuery(id+"F2.wireOp",EDGE,"E398.trimOffspring");Q25=makeQuery(id+"F2.imprint","IMPRINT",FACE,{"disambiguationData":[TD([[makeQuery(id+"F2.imprint","IMPRINT",EDGE,{"derivedFrom":subQ3}),-1.0]])]});}
            var Q26;
            {var subQ0=sQuery(id+"F2.wireOp",EDGE,"E400.trimOffspring");Q26=makeQuery(id+"F2.imprint","IMPRINT",FACE,{"disambiguationData":[TD([[makeQuery(id+"F2.imprint","IMPRINT",EDGE,{"derivedFrom":subQ0}),-1.0]])]});}
            var Q27;
            {var subQ4=sQuery(id+"F2.wireOp",EDGE,"E403.trimOffspring");var subQ10=makeQuery(id+"F2.imprint","IMPRINT",VERTEX,{"derivedFrom":subQ4});Q27=makeQuery(id+"F2.imprint","IMPRINT",FACE,{"disambiguationData":[TD([[makeQuery(id+"F2.imprint","IMPRINT",EDGE,{"disambiguationData":[TD([[subQ10,1.0]])],"derivedFrom":subQ4}),-1.0]])]});}
            var Q28;
            {var subQ5=sQuery(id+"F2.wireOp",EDGE,"E374");Q28=makeQuery(id+"F2.imprint","IMPRINT",FACE,{"disambiguationData":[TD([[makeQuery(id+"F2.imprint","IMPRINT",EDGE,{"derivedFrom":subQ5}),1.0]])]});}
            var Q29;
            {var subQ4=sQuery(id+"F2.wireOp",EDGE,"E405.trimOffspring");var subQ8=makeQuery(id+"F2.imprint","IMPRINT",VERTEX,{"derivedFrom":subQ4});Q29=makeQuery(id+"F2.imprint","IMPRINT",FACE,{"disambiguationData":[TD([[makeQuery(id+"F2.imprint","IMPRINT",EDGE,{"disambiguationData":[TD([[subQ8,1.0]])],"derivedFrom":subQ4}),-1.0]])]});}
            var Q30;
            {var subQ7=sQuery(id+"F2.wireOp",EDGE,"E318");var subQ8=makeQuery(id+"F2.imprint","IMPRINT",VERTEX,{"derivedFrom":subQ7});Q30=makeQuery(id+"F2.imprint","IMPRINT",FACE,{"disambiguationData":[TD([[makeQuery(id+"F2.imprint","IMPRINT",EDGE,{"disambiguationData":[TD([[subQ8,1.0]])],"derivedFrom":subQ7}),1.0]])]});}
            var Q31;
            {var subQ1=sQuery(id+"F2.wireOp",EDGE,"E306");var subQ6=makeQuery(id+"F2.imprint","IMPRINT",VERTEX,{"derivedFrom":subQ1});Q31=makeQuery(id+"F2.imprint","IMPRINT",FACE,{"disambiguationData":[TD([[makeQuery(id+"F2.imprint","IMPRINT",EDGE,{"disambiguationData":[TD([[subQ6,1.0]])],"derivedFrom":subQ1}),1.0]])]});}
            var Q32;
            {var subQ4=sQuery(id+"F2.wireOp",EDGE,"E387");var subQ5=sQuery(id+"F2.wireOp",EDGE,"E386");var subQ6=makeQuery(id+"F2.imprint","INTERSECT",VERTEX,{"derivedFrom":[subQ5,subQ4]});Q32=makeQuery(id+"F2.imprint","IMPRINT",FACE,{"disambiguationData":[TD([[makeQuery(id+"F2.imprint","IMPRINT",EDGE,{"disambiguationData":[TD([[subQ6,-1.0]])],"derivedFrom":subQ5}),1.0]])]});}
            var Q33;
            {var subQ6=sQuery(id+"F2.wireOp",EDGE,"E191");var subQ8=sQuery(id+"F2.wireOp",EDGE,"E213");var subQ9=makeQuery(id+"F2.imprint","INTERSECT",VERTEX,{"derivedFrom":[subQ6,subQ8]});Q33=makeQuery(id+"F2.imprint","IMPRINT",FACE,{"disambiguationData":[TD([[makeQuery(id+"F2.imprint","IMPRINT",EDGE,{"disambiguationData":[TD([[subQ9,-1.0]])],"derivedFrom":subQ6}),1.0]])]});}
            var Q34;
            {var subQ4=sQuery(id+"F2.wireOp",EDGE,"E203");var subQ5=makeQuery(id+"F2.imprint","IMPRINT",VERTEX,{"derivedFrom":subQ4});Q34=makeQuery(id+"F2.imprint","IMPRINT",FACE,{"disambiguationData":[TD([[makeQuery(id+"F2.imprint","IMPRINT",EDGE,{"disambiguationData":[TD([[subQ5,1.0]])],"derivedFrom":subQ4}),1.0]])]});}
            var Q35;
            {var subQ4=sQuery(id+"F2.wireOp",EDGE,"E87");var subQ5=makeQuery(id+"F2.imprint","IMPRINT",VERTEX,{"derivedFrom":subQ4});Q35=makeQuery(id+"F2.imprint","IMPRINT",FACE,{"disambiguationData":[TD([[makeQuery(id+"F2.imprint","IMPRINT",EDGE,{"disambiguationData":[TD([[subQ5,1.0]])],"derivedFrom":subQ4}),1.0]])]});}
            extrude(context, id + "F4", {"entities" : qUnion([Q0, Q1, Q2, Q3, Q4, Q5, Q6, Q7, Q8, Q9, Q10, Q11, Q12, Q13, Q14, Q15, Q16, Q17, Q18, Q19, Q20, Q21, Q22, Q23, Q24, Q25, Q26, Q27, Q28, Q29, Q30, Q31, Q32, Q33, Q34, Q35]), "operationType" : NewBodyOperationType.REMOVE, "depth" : 254 * mm, "offsetDistance" : 25.4 * mm, "hasSecondDirection" : true, "secondDirectionOppositeDirection" : true, "secondDirectionDepth" : 254 * mm});
        }
    });
